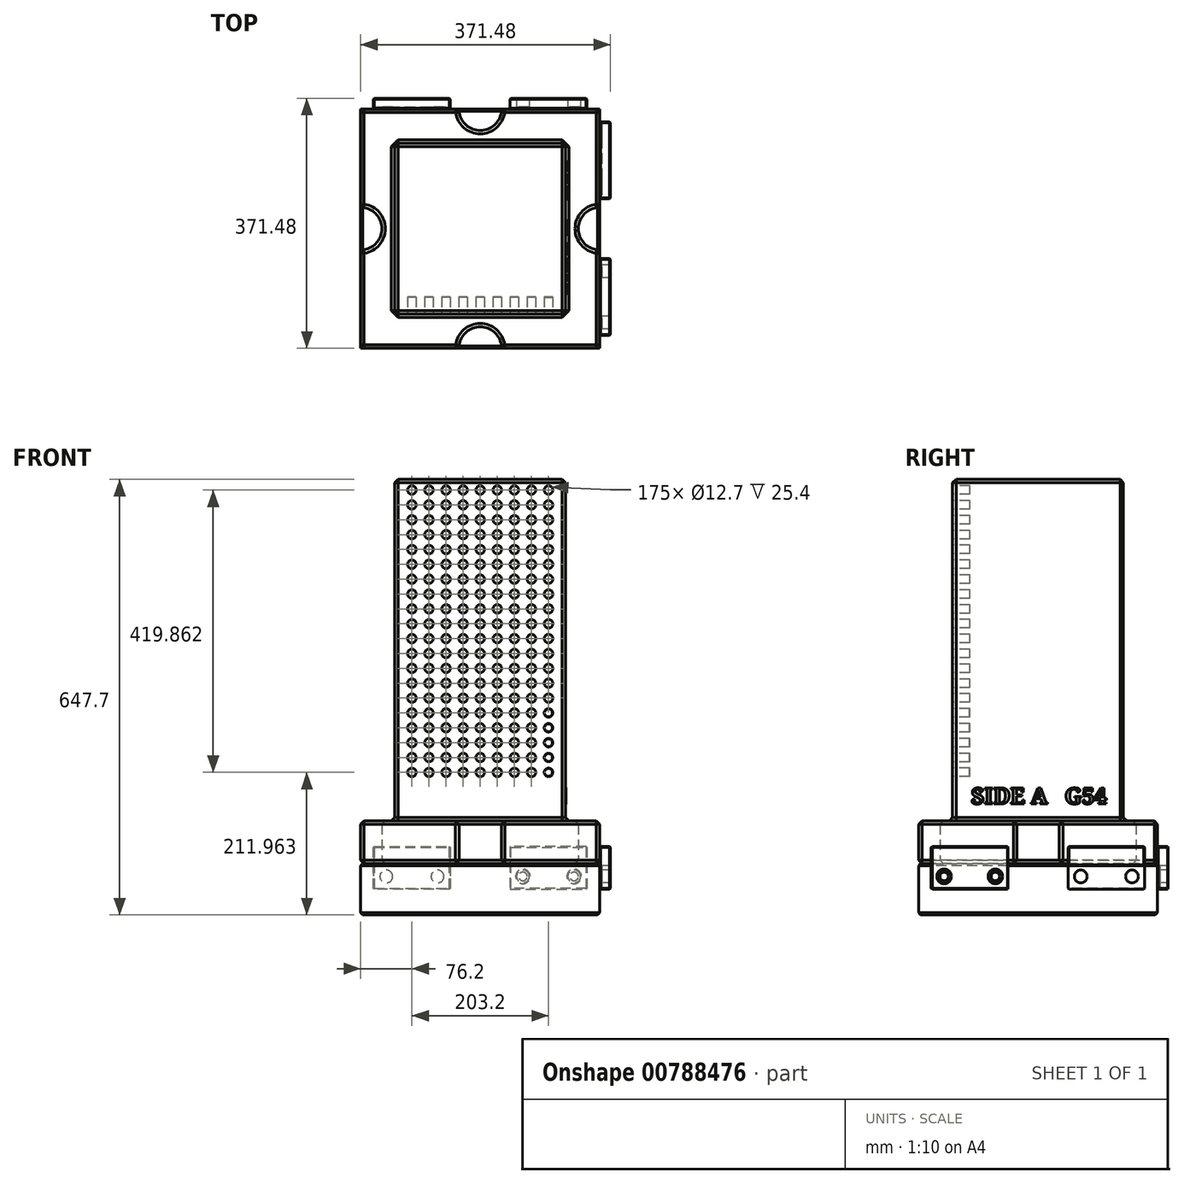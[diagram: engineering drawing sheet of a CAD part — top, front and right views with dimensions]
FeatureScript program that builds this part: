
annotation { "Feature Type Name" : "Feature", "Feature Type Description" : "" }
export const myFeature = defineFeature(function(context is Context, id is Id, definition is map)
    precondition{}
    {
        {
            var Q0;
            Q0=qCreatedBy(makeId("Top.planeOp"),FACE);
            var sketch = newSketch(context, id + "F0", { "sketchPlane" : qUnion([Q0])});
            skLineSegment(sketch, "E0.bottom", {"start": v(-127, -127) * mm, "end": v(127, -127) * mm});
            skLineSegment(sketch, "E0.top", {"start": v(-127, 127) * mm, "end": v(127, 127) * mm});
            skLineSegment(sketch, "E0.left", {"start": v(-127, -127) * mm, "end": v(-127, 127) * mm});
            skLineSegment(sketch, "E0.right", {"start": v(127, -127) * mm, "end": v(127, 127) * mm});
            skPoint(sketch, "E0.middle", {"position": v(0, 0) * mm});
            skLineSegment(sketch, "E1.bottom", {"start": v(-177.8, -177.8) * mm, "end": v(177.8, -177.8) * mm});
            skLineSegment(sketch, "E1.top", {"start": v(-177.8, 177.8) * mm, "end": v(177.8, 177.8) * mm});
            skLineSegment(sketch, "E1.left", {"start": v(-177.8, -177.8) * mm, "end": v(-177.8, 177.8) * mm});
            skLineSegment(sketch, "E1.right", {"start": v(177.8, -177.8) * mm, "end": v(177.8, 177.8) * mm});
            skSolve(sketch);
        }
        {
            var Q0;
            Q0=makeQuery(id+"F0.imprint","IMPRINT",FACE,{"disambiguationData":[TD([[makeQuery(id+"F0.imprint","IMPRINT",EDGE,{"derivedFrom":sQuery(id+"F0.wireOp",EDGE,"E0.bottom")}),1.0]])]});
            extrude(context, id + "F1", {"entities" : qUnion([Q0]), "depth" : 508 * mm});
        }
        {
            var Q0;
            Q0=makeQuery(id+"F0.imprint","IMPRINT",FACE,{"disambiguationData":[TD([[makeQuery(id+"F0.imprint","IMPRINT",EDGE,{"derivedFrom":sQuery(id+"F0.wireOp",EDGE,"E0.bottom")}),-1.0]])]});
            var Q1;
            Q1=makeQuery(id+"F0.imprint","IMPRINT",FACE,{"disambiguationData":[TD([[makeQuery(id+"F0.imprint","IMPRINT",EDGE,{"derivedFrom":sQuery(id+"F0.wireOp",EDGE,"E0.bottom")}),1.0]])]});
            extrude(context, id + "F2", {"entities" : qUnion([Q0, Q1]), "operationType" : NewBodyOperationType.ADD, "oppositeDirection" : true, "depth" : 63.5 * mm});
        }
        {
            var Q0;
            Q0=makeQuery(id+"F2.opExtrude","CAP_FACE",FACE,{"disambiguationData":[OSD([sQuery(id+"F0.wireOp",EDGE,"E1.bottom"),sQuery(id+"F0.wireOp",EDGE,"E1.top"),sQuery(id+"F0.wireOp",EDGE,"E1.left"),sQuery(id+"F0.wireOp",EDGE,"E1.right")])],"isStart":false});
            var sketch = newSketch(context, id + "F3", { "sketchPlane" : qUnion([Q0])});
            skCircle(sketch, "E2", {"center": v(-177.8, 0) * mm, "radius": 31.75 * mm});
            skCircle(sketch, "E3", {"center": v(177.8, 0) * mm, "radius": 31.75 * mm});
            skCircle(sketch, "E4", {"center": v(0, -177.8) * mm, "radius": 31.75 * mm});
            skCircle(sketch, "E5", {"center": v(0, 177.8) * mm, "radius": 31.75 * mm});
            skSolve(sketch);
        }
        {
            var Q0;
            {var subQ0=sQuery(id+"F3.wireOp",EDGE,"E5");var subQ1=makeQuery(id+"F2.opExtrude","CAP_EDGE",EDGE,{"disambiguationData":[OSD([sQuery(id+"F0.wireOp",EDGE,"E1.bottom")])],"isStart":false});var subQ2=makeQuery(id+"F3.imprint","INTERSECT",VERTEX,{"disambiguationData":[OD(0.0)],"derivedFrom":[subQ1,subQ0]});Q0=makeQuery(id+"F3.imprint","IMPRINT",FACE,{"disambiguationData":[TD([[makeQuery(id+"F3.imprint","IMPRINT",EDGE,{"disambiguationData":[TD([[subQ2,-1.0]])],"derivedFrom":subQ0}),1.0]])]});}
            var Q1;
            {var subQ0=sQuery(id+"F3.wireOp",EDGE,"E3");var subQ1=makeQuery(id+"F2.opExtrude","CAP_EDGE",EDGE,{"disambiguationData":[OSD([sQuery(id+"F0.wireOp",EDGE,"E1.right")])],"isStart":false});var subQ2=makeQuery(id+"F3.imprint","INTERSECT",VERTEX,{"disambiguationData":[OD(0.0)],"derivedFrom":[subQ1,subQ0]});Q1=makeQuery(id+"F3.imprint","IMPRINT",FACE,{"disambiguationData":[TD([[makeQuery(id+"F3.imprint","IMPRINT",EDGE,{"disambiguationData":[TD([[subQ2,-1.0]])],"derivedFrom":subQ0}),1.0]])]});}
            var Q2;
            {var subQ0=sQuery(id+"F3.wireOp",EDGE,"E2");var subQ1=makeQuery(id+"F2.opExtrude","CAP_EDGE",EDGE,{"disambiguationData":[OSD([sQuery(id+"F0.wireOp",EDGE,"E1.left")])],"isStart":false});var subQ2=makeQuery(id+"F3.imprint","INTERSECT",VERTEX,{"disambiguationData":[OD(0.0)],"derivedFrom":[subQ1,subQ0]});Q2=makeQuery(id+"F3.imprint","IMPRINT",FACE,{"disambiguationData":[TD([[makeQuery(id+"F3.imprint","IMPRINT",EDGE,{"disambiguationData":[TD([[subQ2,1.0]])],"derivedFrom":subQ0}),1.0]])]});}
            var Q3;
            {var subQ0=sQuery(id+"F3.wireOp",EDGE,"E4");var subQ1=makeQuery(id+"F2.opExtrude","CAP_EDGE",EDGE,{"disambiguationData":[OSD([sQuery(id+"F0.wireOp",EDGE,"E1.top")])],"isStart":false});var subQ2=makeQuery(id+"F3.imprint","INTERSECT",VERTEX,{"disambiguationData":[OD(0.0)],"derivedFrom":[subQ1,subQ0]});Q3=makeQuery(id+"F3.imprint","IMPRINT",FACE,{"disambiguationData":[TD([[makeQuery(id+"F3.imprint","IMPRINT",EDGE,{"disambiguationData":[TD([[subQ2,1.0]])],"derivedFrom":subQ0}),1.0]])]});}
            var Q4;
            Q4=makeQuery(id+"F2.opExtrude","CAP_FACE",FACE,{"disambiguationData":[OSD([sQuery(id+"F0.wireOp",EDGE,"E1.bottom"),sQuery(id+"F0.wireOp",EDGE,"E1.top"),sQuery(id+"F0.wireOp",EDGE,"E1.left"),sQuery(id+"F0.wireOp",EDGE,"E1.right")])],"isStart":true});
            extrude(context, id + "F4", {"entities" : qUnion([Q0, Q1, Q2, Q3]), "operationType" : NewBodyOperationType.REMOVE, "endBound" : BoundingType.UP_TO_SURFACE, "oppositeDirection" : true, "endBoundEntityFace" : qUnion([Q4]), "depth" : 25.4 * mm});
        }
        {
            var Q0;
            Q0=makeQuery(id+"F1.opExtrude","CAP_FACE",FACE,{"disambiguationData":[OSD([sQuery(id+"F0.wireOp",EDGE,"E0.bottom"),sQuery(id+"F0.wireOp",EDGE,"E0.top"),sQuery(id+"F0.wireOp",EDGE,"E0.left"),sQuery(id+"F0.wireOp",EDGE,"E0.right")])],"isStart":false});
            var Q1;
            Q1=makeQuery(id+"F1.opExtrude","SWEPT_FACE",FACE,{"disambiguationData":[OSD([sQuery(id+"F0.wireOp",EDGE,"E0.right")])]});
            var Q2;
            Q2=makeQuery(id+"F1.opExtrude","SWEPT_FACE",FACE,{"disambiguationData":[OSD([sQuery(id+"F0.wireOp",EDGE,"E0.top")])]});
            var Q3;
            Q3=makeQuery(id+"F1.opExtrude","SWEPT_FACE",FACE,{"disambiguationData":[OSD([sQuery(id+"F0.wireOp",EDGE,"E0.left")])]});
            var Q4;
            Q4=makeQuery(id+"F1.opExtrude","SWEPT_FACE",FACE,{"disambiguationData":[OSD([sQuery(id+"F0.wireOp",EDGE,"E0.bottom")])]});
            var Q5;
            {var subQ1=sQuery(id+"F0.wireOp",EDGE,"E1.left");var subQ3=sQuery(id+"F0.wireOp",EDGE,"E1.bottom");Q5=makeQuery(id+"F4.boolean.opBoolean","SPLIT",FACE,{"disambiguationData":[TD([makeQuery(id+"F2.opExtrude","SWEPT_FACE",FACE,{"disambiguationData":[OSD([subQ1])]})])],"derivedFrom":makeQuery(id+"F2.opExtrude","SWEPT_FACE",FACE,{"disambiguationData":[OSD([subQ3])]})});}
            var Q6;
            {var subQ0=sQuery(id+"F0.wireOp",EDGE,"E1.right");var subQ3=sQuery(id+"F0.wireOp",EDGE,"E1.bottom");Q6=makeQuery(id+"F4.boolean.opBoolean","SPLIT",FACE,{"disambiguationData":[TD([makeQuery(id+"F2.opExtrude","SWEPT_FACE",FACE,{"disambiguationData":[OSD([subQ0])]})])],"derivedFrom":makeQuery(id+"F2.opExtrude","SWEPT_FACE",FACE,{"disambiguationData":[OSD([subQ3])]})});}
            var Q7;
            Q7=makeQuery(id+"F4.boolean.opBoolean","COPY",FACE,{"derivedFrom":makeQuery(id+"F4.opExtrude","SWEPT_FACE",FACE,{"disambiguationData":[OSD([sQuery(id+"F3.wireOp",EDGE,"E5")])]})});
            var Q8;
            Q8=makeQuery(id+"F4.boolean.opBoolean","COPY",FACE,{"derivedFrom":makeQuery(id+"F4.opExtrude","SWEPT_FACE",FACE,{"disambiguationData":[OSD([sQuery(id+"F3.wireOp",EDGE,"E3")])]})});
            var Q9;
            {var subQ0=sQuery(id+"F0.wireOp",EDGE,"E1.bottom");var subQ1=sQuery(id+"F0.wireOp",EDGE,"E1.right");Q9=makeQuery(id+"F4.boolean.opBoolean","SPLIT",FACE,{"disambiguationData":[TD([makeQuery(id+"F2.opExtrude","SWEPT_FACE",FACE,{"disambiguationData":[OSD([subQ0])]})])],"derivedFrom":makeQuery(id+"F2.opExtrude","SWEPT_FACE",FACE,{"disambiguationData":[OSD([subQ1])]})});}
            var Q10;
            {var subQ0=sQuery(id+"F0.wireOp",EDGE,"E1.right");var subQ2=sQuery(id+"F0.wireOp",EDGE,"E1.top");Q10=makeQuery(id+"F4.boolean.opBoolean","SPLIT",FACE,{"disambiguationData":[TD([makeQuery(id+"F2.opExtrude","SWEPT_FACE",FACE,{"disambiguationData":[OSD([subQ2])]})])],"derivedFrom":makeQuery(id+"F2.opExtrude","SWEPT_FACE",FACE,{"disambiguationData":[OSD([subQ0])]})});}
            var Q11;
            {var subQ0=sQuery(id+"F0.wireOp",EDGE,"E1.right");var subQ2=sQuery(id+"F0.wireOp",EDGE,"E1.top");Q11=makeQuery(id+"F4.boolean.opBoolean","SPLIT",FACE,{"disambiguationData":[TD([makeQuery(id+"F2.opExtrude","SWEPT_FACE",FACE,{"disambiguationData":[OSD([subQ0])]})])],"derivedFrom":makeQuery(id+"F2.opExtrude","SWEPT_FACE",FACE,{"disambiguationData":[OSD([subQ2])]})});}
            var Q12;
            Q12=makeQuery(id+"F4.boolean.opBoolean","COPY",FACE,{"derivedFrom":makeQuery(id+"F4.opExtrude","SWEPT_FACE",FACE,{"disambiguationData":[OSD([sQuery(id+"F3.wireOp",EDGE,"E4")])]})});
            var Q13;
            {var subQ1=sQuery(id+"F0.wireOp",EDGE,"E1.left");var subQ2=sQuery(id+"F0.wireOp",EDGE,"E1.top");Q13=makeQuery(id+"F4.boolean.opBoolean","SPLIT",FACE,{"disambiguationData":[TD([makeQuery(id+"F2.opExtrude","SWEPT_FACE",FACE,{"disambiguationData":[OSD([subQ1])]})])],"derivedFrom":makeQuery(id+"F2.opExtrude","SWEPT_FACE",FACE,{"disambiguationData":[OSD([subQ2])]})});}
            var Q14;
            {var subQ1=sQuery(id+"F0.wireOp",EDGE,"E1.left");var subQ2=sQuery(id+"F0.wireOp",EDGE,"E1.top");Q14=makeQuery(id+"F4.boolean.opBoolean","SPLIT",FACE,{"disambiguationData":[TD([makeQuery(id+"F2.opExtrude","SWEPT_FACE",FACE,{"disambiguationData":[OSD([subQ2])]})])],"derivedFrom":makeQuery(id+"F2.opExtrude","SWEPT_FACE",FACE,{"disambiguationData":[OSD([subQ1])]})});}
            var Q15;
            Q15=makeQuery(id+"F4.boolean.opBoolean","COPY",FACE,{"derivedFrom":makeQuery(id+"F4.opExtrude","SWEPT_FACE",FACE,{"disambiguationData":[OSD([sQuery(id+"F3.wireOp",EDGE,"E2")])]})});
            var Q16;
            {var subQ0=sQuery(id+"F0.wireOp",EDGE,"E1.bottom");var subQ2=sQuery(id+"F0.wireOp",EDGE,"E1.left");Q16=makeQuery(id+"F4.boolean.opBoolean","SPLIT",FACE,{"disambiguationData":[TD([makeQuery(id+"F2.opExtrude","SWEPT_FACE",FACE,{"disambiguationData":[OSD([subQ0])]})])],"derivedFrom":makeQuery(id+"F2.opExtrude","SWEPT_FACE",FACE,{"disambiguationData":[OSD([subQ2])]})});}
            chamfer(context, id + "F5", {"entities" : qUnion([Q0, Q1, Q2, Q3, Q4, Q5, Q6, Q7, Q8, Q9, Q10, Q11, Q12, Q13, Q14, Q15, Q16]), "width" : 5.08 * mm, "tangentPropagation" : true});
        }
        {
            var Q0;
            Q0=makeQuery(id+"F1.opExtrude","SWEPT_FACE",FACE,{"disambiguationData":[OSD([sQuery(id+"F0.wireOp",EDGE,"E0.bottom")])]});
            var sketch = newSketch(context, id + "F6", { "sketchPlane" : qUnion([Q0])});
            skCircle(sketch, "E6", {"center": v(-101.6, 492.13) * mm, "radius": 6.35 * mm});
            skLineSegment(sketch, "E7", {"start": v(0, 0) * mm, "end": v(0, 678.57) * mm, "construction": true});
            skCircle(sketch, "E8.0.1.0", {"center": v(-101.6, 470.03) * mm, "radius": 6.35 * mm});
            skCircle(sketch, "E8.0.2.0", {"center": v(-101.6, 447.93) * mm, "radius": 6.35 * mm});
            skCircle(sketch, "E8.0.3.0", {"center": v(-101.6, 425.83) * mm, "radius": 6.35 * mm});
            skCircle(sketch, "E8.0.4.0", {"center": v(-101.6, 403.73) * mm, "radius": 6.35 * mm});
            skCircle(sketch, "E8.0.5.0", {"center": v(-101.6, 381.63) * mm, "radius": 6.35 * mm});
            skCircle(sketch, "E8.0.6.0", {"center": v(-101.6, 359.54) * mm, "radius": 6.35 * mm});
            skCircle(sketch, "E8.0.7.0", {"center": v(-101.6, 337.44) * mm, "radius": 6.35 * mm});
            skCircle(sketch, "E8.0.8.0", {"center": v(-101.6, 315.34) * mm, "radius": 6.35 * mm});
            skCircle(sketch, "E8.0.9.0", {"center": v(-101.6, 293.24) * mm, "radius": 6.35 * mm});
            skCircle(sketch, "E8.0.10.0", {"center": v(-101.6, 271.14) * mm, "radius": 6.35 * mm});
            skCircle(sketch, "E8.0.11.0", {"center": v(-101.6, 249.05) * mm, "radius": 6.35 * mm});
            skCircle(sketch, "E8.0.12.0", {"center": v(-101.6, 226.95) * mm, "radius": 6.35 * mm});
            skCircle(sketch, "E8.0.13.0", {"center": v(-101.6, 204.85) * mm, "radius": 6.35 * mm});
            skCircle(sketch, "E8.0.14.0", {"center": v(-101.6, 182.75) * mm, "radius": 6.35 * mm});
            skCircle(sketch, "E8.1.0.0", {"center": v(-76.2, 492.13) * mm, "radius": 6.35 * mm});
            skCircle(sketch, "E8.1.1.0", {"center": v(-76.2, 470.03) * mm, "radius": 6.35 * mm});
            skCircle(sketch, "E8.1.2.0", {"center": v(-76.2, 447.93) * mm, "radius": 6.35 * mm});
            skCircle(sketch, "E8.1.3.0", {"center": v(-76.2, 425.83) * mm, "radius": 6.35 * mm});
            skCircle(sketch, "E8.1.4.0", {"center": v(-76.2, 403.73) * mm, "radius": 6.35 * mm});
            skCircle(sketch, "E8.1.5.0", {"center": v(-76.2, 381.63) * mm, "radius": 6.35 * mm});
            skCircle(sketch, "E8.1.6.0", {"center": v(-76.2, 359.54) * mm, "radius": 6.35 * mm});
            skCircle(sketch, "E8.1.7.0", {"center": v(-76.2, 337.44) * mm, "radius": 6.35 * mm});
            skCircle(sketch, "E8.1.8.0", {"center": v(-76.2, 315.34) * mm, "radius": 6.35 * mm});
            skCircle(sketch, "E8.1.9.0", {"center": v(-76.2, 293.24) * mm, "radius": 6.35 * mm});
            skCircle(sketch, "E8.1.10.0", {"center": v(-76.2, 271.14) * mm, "radius": 6.35 * mm});
            skCircle(sketch, "E8.1.11.0", {"center": v(-76.2, 249.05) * mm, "radius": 6.35 * mm});
            skCircle(sketch, "E8.1.12.0", {"center": v(-76.2, 226.95) * mm, "radius": 6.35 * mm});
            skCircle(sketch, "E8.1.13.0", {"center": v(-76.2, 204.85) * mm, "radius": 6.35 * mm});
            skCircle(sketch, "E8.1.14.0", {"center": v(-76.2, 182.75) * mm, "radius": 6.35 * mm});
            skCircle(sketch, "E8.2.0.0", {"center": v(-50.8, 492.13) * mm, "radius": 6.35 * mm});
            skCircle(sketch, "E8.2.1.0", {"center": v(-50.8, 470.03) * mm, "radius": 6.35 * mm});
            skCircle(sketch, "E8.2.2.0", {"center": v(-50.8, 447.93) * mm, "radius": 6.35 * mm});
            skCircle(sketch, "E8.2.3.0", {"center": v(-50.8, 425.83) * mm, "radius": 6.35 * mm});
            skCircle(sketch, "E8.2.4.0", {"center": v(-50.8, 403.73) * mm, "radius": 6.35 * mm});
            skCircle(sketch, "E8.2.5.0", {"center": v(-50.8, 381.63) * mm, "radius": 6.35 * mm});
            skCircle(sketch, "E8.2.6.0", {"center": v(-50.8, 359.54) * mm, "radius": 6.35 * mm});
            skCircle(sketch, "E8.2.7.0", {"center": v(-50.8, 337.44) * mm, "radius": 6.35 * mm});
            skCircle(sketch, "E8.2.8.0", {"center": v(-50.8, 315.34) * mm, "radius": 6.35 * mm});
            skCircle(sketch, "E8.2.9.0", {"center": v(-50.8, 293.24) * mm, "radius": 6.35 * mm});
            skCircle(sketch, "E8.2.10.0", {"center": v(-50.8, 271.14) * mm, "radius": 6.35 * mm});
            skCircle(sketch, "E8.2.11.0", {"center": v(-50.8, 249.05) * mm, "radius": 6.35 * mm});
            skCircle(sketch, "E8.2.12.0", {"center": v(-50.8, 226.95) * mm, "radius": 6.35 * mm});
            skCircle(sketch, "E8.2.13.0", {"center": v(-50.8, 204.85) * mm, "radius": 6.35 * mm});
            skCircle(sketch, "E8.2.14.0", {"center": v(-50.8, 182.75) * mm, "radius": 6.35 * mm});
            skCircle(sketch, "E8.3.0.0", {"center": v(-25.4, 492.13) * mm, "radius": 6.35 * mm});
            skCircle(sketch, "E8.3.1.0", {"center": v(-25.4, 470.03) * mm, "radius": 6.35 * mm});
            skCircle(sketch, "E8.3.2.0", {"center": v(-25.4, 447.93) * mm, "radius": 6.35 * mm});
            skCircle(sketch, "E8.3.3.0", {"center": v(-25.4, 425.83) * mm, "radius": 6.35 * mm});
            skCircle(sketch, "E8.3.4.0", {"center": v(-25.4, 403.73) * mm, "radius": 6.35 * mm});
            skCircle(sketch, "E8.3.5.0", {"center": v(-25.4, 381.63) * mm, "radius": 6.35 * mm});
            skCircle(sketch, "E8.3.6.0", {"center": v(-25.4, 359.54) * mm, "radius": 6.35 * mm});
            skCircle(sketch, "E8.3.7.0", {"center": v(-25.4, 337.44) * mm, "radius": 6.35 * mm});
            skCircle(sketch, "E8.3.8.0", {"center": v(-25.4, 315.34) * mm, "radius": 6.35 * mm});
            skCircle(sketch, "E8.3.9.0", {"center": v(-25.4, 293.24) * mm, "radius": 6.35 * mm});
            skCircle(sketch, "E8.3.10.0", {"center": v(-25.4, 271.14) * mm, "radius": 6.35 * mm});
            skCircle(sketch, "E8.3.11.0", {"center": v(-25.4, 249.05) * mm, "radius": 6.35 * mm});
            skCircle(sketch, "E8.3.12.0", {"center": v(-25.4, 226.95) * mm, "radius": 6.35 * mm});
            skCircle(sketch, "E8.3.13.0", {"center": v(-25.4, 204.85) * mm, "radius": 6.35 * mm});
            skCircle(sketch, "E8.3.14.0", {"center": v(-25.4, 182.75) * mm, "radius": 6.35 * mm});
            skCircle(sketch, "E8.4.0.0", {"center": v(0, 492.13) * mm, "radius": 6.35 * mm});
            skCircle(sketch, "E8.4.1.0", {"center": v(0, 470.03) * mm, "radius": 6.35 * mm});
            skCircle(sketch, "E8.4.2.0", {"center": v(0, 447.93) * mm, "radius": 6.35 * mm});
            skCircle(sketch, "E8.4.3.0", {"center": v(0, 425.83) * mm, "radius": 6.35 * mm});
            skCircle(sketch, "E8.4.4.0", {"center": v(0, 403.73) * mm, "radius": 6.35 * mm});
            skCircle(sketch, "E8.4.5.0", {"center": v(0, 381.63) * mm, "radius": 6.35 * mm});
            skCircle(sketch, "E8.4.6.0", {"center": v(0, 359.54) * mm, "radius": 6.35 * mm});
            skCircle(sketch, "E8.4.7.0", {"center": v(0, 337.44) * mm, "radius": 6.35 * mm});
            skCircle(sketch, "E8.4.8.0", {"center": v(0, 315.34) * mm, "radius": 6.35 * mm});
            skCircle(sketch, "E8.4.9.0", {"center": v(0, 293.24) * mm, "radius": 6.35 * mm});
            skCircle(sketch, "E8.4.10.0", {"center": v(0, 271.14) * mm, "radius": 6.35 * mm});
            skCircle(sketch, "E8.4.11.0", {"center": v(0, 249.05) * mm, "radius": 6.35 * mm});
            skCircle(sketch, "E8.4.12.0", {"center": v(0, 226.95) * mm, "radius": 6.35 * mm});
            skCircle(sketch, "E8.4.13.0", {"center": v(0, 204.85) * mm, "radius": 6.35 * mm});
            skCircle(sketch, "E8.4.14.0", {"center": v(0, 182.75) * mm, "radius": 6.35 * mm});
            skCircle(sketch, "E8.5.0.0", {"center": v(25.4, 492.13) * mm, "radius": 6.35 * mm});
            skCircle(sketch, "E8.5.1.0", {"center": v(25.4, 470.03) * mm, "radius": 6.35 * mm});
            skCircle(sketch, "E8.5.2.0", {"center": v(25.4, 447.93) * mm, "radius": 6.35 * mm});
            skCircle(sketch, "E8.5.3.0", {"center": v(25.4, 425.83) * mm, "radius": 6.35 * mm});
            skCircle(sketch, "E8.5.4.0", {"center": v(25.4, 403.73) * mm, "radius": 6.35 * mm});
            skCircle(sketch, "E8.5.5.0", {"center": v(25.4, 381.63) * mm, "radius": 6.35 * mm});
            skCircle(sketch, "E8.5.6.0", {"center": v(25.4, 359.54) * mm, "radius": 6.35 * mm});
            skCircle(sketch, "E8.5.7.0", {"center": v(25.4, 337.44) * mm, "radius": 6.35 * mm});
            skCircle(sketch, "E8.5.8.0", {"center": v(25.4, 315.34) * mm, "radius": 6.35 * mm});
            skCircle(sketch, "E8.5.9.0", {"center": v(25.4, 293.24) * mm, "radius": 6.35 * mm});
            skCircle(sketch, "E8.5.10.0", {"center": v(25.4, 271.14) * mm, "radius": 6.35 * mm});
            skCircle(sketch, "E8.5.11.0", {"center": v(25.4, 249.05) * mm, "radius": 6.35 * mm});
            skCircle(sketch, "E8.5.12.0", {"center": v(25.4, 226.95) * mm, "radius": 6.35 * mm});
            skCircle(sketch, "E8.5.13.0", {"center": v(25.4, 204.85) * mm, "radius": 6.35 * mm});
            skCircle(sketch, "E8.5.14.0", {"center": v(25.4, 182.75) * mm, "radius": 6.35 * mm});
            skCircle(sketch, "E8.6.0.0", {"center": v(50.8, 492.13) * mm, "radius": 6.35 * mm});
            skCircle(sketch, "E8.6.1.0", {"center": v(50.8, 470.03) * mm, "radius": 6.35 * mm});
            skCircle(sketch, "E8.6.2.0", {"center": v(50.8, 447.93) * mm, "radius": 6.35 * mm});
            skCircle(sketch, "E8.6.3.0", {"center": v(50.8, 425.83) * mm, "radius": 6.35 * mm});
            skCircle(sketch, "E8.6.4.0", {"center": v(50.8, 403.73) * mm, "radius": 6.35 * mm});
            skCircle(sketch, "E8.6.5.0", {"center": v(50.8, 381.63) * mm, "radius": 6.35 * mm});
            skCircle(sketch, "E8.6.6.0", {"center": v(50.8, 359.54) * mm, "radius": 6.35 * mm});
            skCircle(sketch, "E8.6.7.0", {"center": v(50.8, 337.44) * mm, "radius": 6.35 * mm});
            skCircle(sketch, "E8.6.8.0", {"center": v(50.8, 315.34) * mm, "radius": 6.35 * mm});
            skCircle(sketch, "E8.6.9.0", {"center": v(50.8, 293.24) * mm, "radius": 6.35 * mm});
            skCircle(sketch, "E8.6.10.0", {"center": v(50.8, 271.14) * mm, "radius": 6.35 * mm});
            skCircle(sketch, "E8.6.11.0", {"center": v(50.8, 249.05) * mm, "radius": 6.35 * mm});
            skCircle(sketch, "E8.6.12.0", {"center": v(50.8, 226.95) * mm, "radius": 6.35 * mm});
            skCircle(sketch, "E8.6.13.0", {"center": v(50.8, 204.85) * mm, "radius": 6.35 * mm});
            skCircle(sketch, "E8.6.14.0", {"center": v(50.8, 182.75) * mm, "radius": 6.35 * mm});
            skCircle(sketch, "E8.7.0.0", {"center": v(76.2, 492.13) * mm, "radius": 6.35 * mm});
            skCircle(sketch, "E8.7.1.0", {"center": v(76.2, 470.03) * mm, "radius": 6.35 * mm});
            skCircle(sketch, "E8.7.2.0", {"center": v(76.2, 447.93) * mm, "radius": 6.35 * mm});
            skCircle(sketch, "E8.7.3.0", {"center": v(76.2, 425.83) * mm, "radius": 6.35 * mm});
            skCircle(sketch, "E8.7.4.0", {"center": v(76.2, 403.73) * mm, "radius": 6.35 * mm});
            skCircle(sketch, "E8.7.5.0", {"center": v(76.2, 381.63) * mm, "radius": 6.35 * mm});
            skCircle(sketch, "E8.7.6.0", {"center": v(76.2, 359.54) * mm, "radius": 6.35 * mm});
            skCircle(sketch, "E8.7.7.0", {"center": v(76.2, 337.44) * mm, "radius": 6.35 * mm});
            skCircle(sketch, "E8.7.8.0", {"center": v(76.2, 315.34) * mm, "radius": 6.35 * mm});
            skCircle(sketch, "E8.7.9.0", {"center": v(76.2, 293.24) * mm, "radius": 6.35 * mm});
            skCircle(sketch, "E8.7.10.0", {"center": v(76.2, 271.14) * mm, "radius": 6.35 * mm});
            skCircle(sketch, "E8.7.11.0", {"center": v(76.2, 249.05) * mm, "radius": 6.35 * mm});
            skCircle(sketch, "E8.7.12.0", {"center": v(76.2, 226.95) * mm, "radius": 6.35 * mm});
            skCircle(sketch, "E8.7.13.0", {"center": v(76.2, 204.85) * mm, "radius": 6.35 * mm});
            skCircle(sketch, "E8.7.14.0", {"center": v(76.2, 182.75) * mm, "radius": 6.35 * mm});
            skCircle(sketch, "E8.8.0.0", {"center": v(101.6, 492.13) * mm, "radius": 6.35 * mm});
            skCircle(sketch, "E8.8.1.0", {"center": v(101.6, 470.03) * mm, "radius": 6.35 * mm});
            skCircle(sketch, "E8.8.2.0", {"center": v(101.6, 447.93) * mm, "radius": 6.35 * mm});
            skCircle(sketch, "E8.8.3.0", {"center": v(101.6, 425.83) * mm, "radius": 6.35 * mm});
            skCircle(sketch, "E8.8.4.0", {"center": v(101.6, 403.73) * mm, "radius": 6.35 * mm});
            skCircle(sketch, "E8.8.5.0", {"center": v(101.6, 381.63) * mm, "radius": 6.35 * mm});
            skCircle(sketch, "E8.8.6.0", {"center": v(101.6, 359.54) * mm, "radius": 6.35 * mm});
            skCircle(sketch, "E8.8.7.0", {"center": v(101.6, 337.44) * mm, "radius": 6.35 * mm});
            skCircle(sketch, "E8.8.8.0", {"center": v(101.6, 315.34) * mm, "radius": 6.35 * mm});
            skCircle(sketch, "E8.8.9.0", {"center": v(101.6, 293.24) * mm, "radius": 6.35 * mm});
            skCircle(sketch, "E8.8.10.0", {"center": v(101.6, 271.14) * mm, "radius": 6.35 * mm});
            skCircle(sketch, "E8.8.11.0", {"center": v(101.6, 249.05) * mm, "radius": 6.35 * mm});
            skCircle(sketch, "E8.8.12.0", {"center": v(101.6, 226.95) * mm, "radius": 6.35 * mm});
            skCircle(sketch, "E8.8.13.0", {"center": v(101.6, 204.85) * mm, "radius": 6.35 * mm});
            skCircle(sketch, "E8.8.14.0", {"center": v(101.6, 182.75) * mm, "radius": 6.35 * mm});
            skLineSegment(sketch, "E8.direction1", {"start": v(-101.6, 492.13) * mm, "end": v(-76.2, 492.13) * mm, "construction": true});
            skLineSegment(sketch, "E8.direction2", {"start": v(-101.6, 492.13) * mm, "end": v(-101.6, 470.03) * mm, "construction": true});
            skCircle(sketch, "E9.0.0.15", {"center": v(-101.6, 160.65) * mm, "radius": 6.35 * mm});
            skCircle(sketch, "E9.0.0.16", {"center": v(-101.6, 138.56) * mm, "radius": 6.35 * mm});
            skCircle(sketch, "E9.0.0.17", {"center": v(-101.6, 116.46) * mm, "radius": 6.35 * mm});
            skCircle(sketch, "E9.0.0.18", {"center": v(-101.6, 94.36) * mm, "radius": 6.35 * mm});
            skCircle(sketch, "E9.0.0.19", {"center": v(-101.6, 72.26) * mm, "radius": 6.35 * mm});
            skCircle(sketch, "E9.0.1.15", {"center": v(-76.2, 160.65) * mm, "radius": 6.35 * mm});
            skCircle(sketch, "E9.0.1.16", {"center": v(-76.2, 138.56) * mm, "radius": 6.35 * mm});
            skCircle(sketch, "E9.0.1.17", {"center": v(-76.2, 116.46) * mm, "radius": 6.35 * mm});
            skCircle(sketch, "E9.0.1.18", {"center": v(-76.2, 94.36) * mm, "radius": 6.35 * mm});
            skCircle(sketch, "E9.0.1.19", {"center": v(-76.2, 72.26) * mm, "radius": 6.35 * mm});
            skCircle(sketch, "E9.0.2.15", {"center": v(-50.8, 160.65) * mm, "radius": 6.35 * mm});
            skCircle(sketch, "E9.0.2.16", {"center": v(-50.8, 138.56) * mm, "radius": 6.35 * mm});
            skCircle(sketch, "E9.0.2.17", {"center": v(-50.8, 116.46) * mm, "radius": 6.35 * mm});
            skCircle(sketch, "E9.0.2.18", {"center": v(-50.8, 94.36) * mm, "radius": 6.35 * mm});
            skCircle(sketch, "E9.0.2.19", {"center": v(-50.8, 72.26) * mm, "radius": 6.35 * mm});
            skCircle(sketch, "E9.0.3.15", {"center": v(-25.4, 160.65) * mm, "radius": 6.35 * mm});
            skCircle(sketch, "E9.0.3.16", {"center": v(-25.4, 138.56) * mm, "radius": 6.35 * mm});
            skCircle(sketch, "E9.0.3.17", {"center": v(-25.4, 116.46) * mm, "radius": 6.35 * mm});
            skCircle(sketch, "E9.0.3.18", {"center": v(-25.4, 94.36) * mm, "radius": 6.35 * mm});
            skCircle(sketch, "E9.0.3.19", {"center": v(-25.4, 72.26) * mm, "radius": 6.35 * mm});
            skCircle(sketch, "E9.0.4.15", {"center": v(0, 160.65) * mm, "radius": 6.35 * mm});
            skCircle(sketch, "E9.0.4.16", {"center": v(0, 138.56) * mm, "radius": 6.35 * mm});
            skCircle(sketch, "E9.0.4.17", {"center": v(0, 116.46) * mm, "radius": 6.35 * mm});
            skCircle(sketch, "E9.0.4.18", {"center": v(0, 94.36) * mm, "radius": 6.35 * mm});
            skCircle(sketch, "E9.0.4.19", {"center": v(0, 72.26) * mm, "radius": 6.35 * mm});
            skCircle(sketch, "E9.0.5.15", {"center": v(25.4, 160.65) * mm, "radius": 6.35 * mm});
            skCircle(sketch, "E9.0.5.16", {"center": v(25.4, 138.56) * mm, "radius": 6.35 * mm});
            skCircle(sketch, "E9.0.5.17", {"center": v(25.4, 116.46) * mm, "radius": 6.35 * mm});
            skCircle(sketch, "E9.0.5.18", {"center": v(25.4, 94.36) * mm, "radius": 6.35 * mm});
            skCircle(sketch, "E9.0.5.19", {"center": v(25.4, 72.26) * mm, "radius": 6.35 * mm});
            skCircle(sketch, "E9.0.6.15", {"center": v(50.8, 160.65) * mm, "radius": 6.35 * mm});
            skCircle(sketch, "E9.0.6.16", {"center": v(50.8, 138.56) * mm, "radius": 6.35 * mm});
            skCircle(sketch, "E9.0.6.17", {"center": v(50.8, 116.46) * mm, "radius": 6.35 * mm});
            skCircle(sketch, "E9.0.6.18", {"center": v(50.8, 94.36) * mm, "radius": 6.35 * mm});
            skCircle(sketch, "E9.0.6.19", {"center": v(50.8, 72.26) * mm, "radius": 6.35 * mm});
            skCircle(sketch, "E9.0.7.15", {"center": v(76.2, 160.65) * mm, "radius": 6.35 * mm});
            skCircle(sketch, "E9.0.7.16", {"center": v(76.2, 138.56) * mm, "radius": 6.35 * mm});
            skCircle(sketch, "E9.0.7.17", {"center": v(76.2, 116.46) * mm, "radius": 6.35 * mm});
            skCircle(sketch, "E9.0.7.18", {"center": v(76.2, 94.36) * mm, "radius": 6.35 * mm});
            skCircle(sketch, "E9.0.7.19", {"center": v(76.2, 72.26) * mm, "radius": 6.35 * mm});
            skCircle(sketch, "E9.0.8.15", {"center": v(101.6, 160.65) * mm, "radius": 6.35 * mm});
            skCircle(sketch, "E9.0.8.16", {"center": v(101.6, 138.56) * mm, "radius": 6.35 * mm});
            skCircle(sketch, "E9.0.8.17", {"center": v(101.6, 116.46) * mm, "radius": 6.35 * mm});
            skCircle(sketch, "E9.0.8.18", {"center": v(101.6, 94.36) * mm, "radius": 6.35 * mm});
            skCircle(sketch, "E9.0.8.19", {"center": v(101.6, 72.26) * mm, "radius": 6.35 * mm});
            skSolve(sketch);
        }
        {
            var Q0;
            Q0=qSketchRegion(id+"F6",true);
            extrude(context, id + "F7", {"entities" : qUnion([Q0]), "operationType" : NewBodyOperationType.REMOVE, "oppositeDirection" : true, "depth" : 25.4 * mm});
        }
        {
            var Q0;
            Q0=makeQuery(id+"F7.boolean.opBoolean","COPY",EDGE,{"derivedFrom":makeQuery(id+"F7.opExtrude","CAP_EDGE",EDGE,{"disambiguationData":[OSD([sQuery(id+"F6.wireOp",EDGE,"E6")])],"isStart":true})});
            var Q1;
            Q1=makeQuery(id+"F7.boolean.opBoolean","COPY",EDGE,{"derivedFrom":makeQuery(id+"F7.opExtrude","CAP_EDGE",EDGE,{"disambiguationData":[OSD([sQuery(id+"F6.wireOp",EDGE,"E8.0.1.0")])],"isStart":true})});
            var Q2;
            Q2=makeQuery(id+"F7.boolean.opBoolean","COPY",EDGE,{"derivedFrom":makeQuery(id+"F7.opExtrude","CAP_EDGE",EDGE,{"disambiguationData":[OSD([sQuery(id+"F6.wireOp",EDGE,"E8.0.2.0")])],"isStart":true})});
            var Q3;
            Q3=makeQuery(id+"F7.boolean.opBoolean","COPY",EDGE,{"derivedFrom":makeQuery(id+"F7.opExtrude","CAP_EDGE",EDGE,{"disambiguationData":[OSD([sQuery(id+"F6.wireOp",EDGE,"E8.0.3.0")])],"isStart":true})});
            var Q4;
            Q4=makeQuery(id+"F7.boolean.opBoolean","COPY",EDGE,{"derivedFrom":makeQuery(id+"F7.opExtrude","CAP_EDGE",EDGE,{"disambiguationData":[OSD([sQuery(id+"F6.wireOp",EDGE,"E8.0.4.0")])],"isStart":true})});
            var Q5;
            Q5=makeQuery(id+"F7.boolean.opBoolean","COPY",EDGE,{"derivedFrom":makeQuery(id+"F7.opExtrude","CAP_EDGE",EDGE,{"disambiguationData":[OSD([sQuery(id+"F6.wireOp",EDGE,"E8.0.6.0")])],"isStart":true})});
            var Q6;
            Q6=makeQuery(id+"F7.boolean.opBoolean","COPY",EDGE,{"derivedFrom":makeQuery(id+"F7.opExtrude","CAP_EDGE",EDGE,{"disambiguationData":[OSD([sQuery(id+"F6.wireOp",EDGE,"E8.0.5.0")])],"isStart":true})});
            var Q7;
            Q7=makeQuery(id+"F7.boolean.opBoolean","COPY",EDGE,{"derivedFrom":makeQuery(id+"F7.opExtrude","CAP_EDGE",EDGE,{"disambiguationData":[OSD([sQuery(id+"F6.wireOp",EDGE,"E8.0.7.0")])],"isStart":true})});
            var Q8;
            Q8=makeQuery(id+"F7.boolean.opBoolean","COPY",EDGE,{"derivedFrom":makeQuery(id+"F7.opExtrude","CAP_EDGE",EDGE,{"disambiguationData":[OSD([sQuery(id+"F6.wireOp",EDGE,"E8.0.8.0")])],"isStart":true})});
            var Q9;
            Q9=makeQuery(id+"F7.boolean.opBoolean","COPY",EDGE,{"derivedFrom":makeQuery(id+"F7.opExtrude","CAP_EDGE",EDGE,{"disambiguationData":[OSD([sQuery(id+"F6.wireOp",EDGE,"E8.0.9.0")])],"isStart":true})});
            var Q10;
            Q10=makeQuery(id+"F7.boolean.opBoolean","COPY",EDGE,{"derivedFrom":makeQuery(id+"F7.opExtrude","CAP_EDGE",EDGE,{"disambiguationData":[OSD([sQuery(id+"F6.wireOp",EDGE,"E8.0.10.0")])],"isStart":true})});
            var Q11;
            Q11=makeQuery(id+"F7.boolean.opBoolean","COPY",EDGE,{"derivedFrom":makeQuery(id+"F7.opExtrude","CAP_EDGE",EDGE,{"disambiguationData":[OSD([sQuery(id+"F6.wireOp",EDGE,"E8.0.11.0")])],"isStart":true})});
            var Q12;
            Q12=makeQuery(id+"F7.boolean.opBoolean","COPY",EDGE,{"derivedFrom":makeQuery(id+"F7.opExtrude","CAP_EDGE",EDGE,{"disambiguationData":[OSD([sQuery(id+"F6.wireOp",EDGE,"E8.0.12.0")])],"isStart":true})});
            var Q13;
            Q13=makeQuery(id+"F7.boolean.opBoolean","COPY",EDGE,{"derivedFrom":makeQuery(id+"F7.opExtrude","CAP_EDGE",EDGE,{"disambiguationData":[OSD([sQuery(id+"F6.wireOp",EDGE,"E8.0.13.0")])],"isStart":true})});
            var Q14;
            Q14=makeQuery(id+"F7.boolean.opBoolean","COPY",EDGE,{"derivedFrom":makeQuery(id+"F7.opExtrude","CAP_EDGE",EDGE,{"disambiguationData":[OSD([sQuery(id+"F6.wireOp",EDGE,"E8.0.14.0")])],"isStart":true})});
            var Q15;
            Q15=makeQuery(id+"F7.boolean.opBoolean","COPY",EDGE,{"derivedFrom":makeQuery(id+"F7.opExtrude","CAP_EDGE",EDGE,{"disambiguationData":[OSD([sQuery(id+"F6.wireOp",EDGE,"E9.0.0.15")])],"isStart":true})});
            var Q16;
            Q16=makeQuery(id+"F7.boolean.opBoolean","COPY",EDGE,{"derivedFrom":makeQuery(id+"F7.opExtrude","CAP_EDGE",EDGE,{"disambiguationData":[OSD([sQuery(id+"F6.wireOp",EDGE,"E9.0.0.16")])],"isStart":true})});
            var Q17;
            Q17=makeQuery(id+"F7.boolean.opBoolean","COPY",EDGE,{"derivedFrom":makeQuery(id+"F7.opExtrude","CAP_EDGE",EDGE,{"disambiguationData":[OSD([sQuery(id+"F6.wireOp",EDGE,"E9.0.0.17")])],"isStart":true})});
            var Q18;
            Q18=makeQuery(id+"F7.boolean.opBoolean","COPY",EDGE,{"derivedFrom":makeQuery(id+"F7.opExtrude","CAP_EDGE",EDGE,{"disambiguationData":[OSD([sQuery(id+"F6.wireOp",EDGE,"E9.0.0.18")])],"isStart":true})});
            var Q19;
            Q19=makeQuery(id+"F7.boolean.opBoolean","COPY",EDGE,{"derivedFrom":makeQuery(id+"F7.opExtrude","CAP_EDGE",EDGE,{"disambiguationData":[OSD([sQuery(id+"F6.wireOp",EDGE,"E9.0.0.19")])],"isStart":true})});
            var Q20;
            Q20=makeQuery(id+"F7.boolean.opBoolean","COPY",EDGE,{"derivedFrom":makeQuery(id+"F7.opExtrude","CAP_EDGE",EDGE,{"disambiguationData":[OSD([sQuery(id+"F6.wireOp",EDGE,"E9.0.7.19")])],"isStart":true})});
            var Q21;
            Q21=makeQuery(id+"F7.boolean.opBoolean","COPY",EDGE,{"derivedFrom":makeQuery(id+"F7.opExtrude","CAP_EDGE",EDGE,{"disambiguationData":[OSD([sQuery(id+"F6.wireOp",EDGE,"E9.0.7.18")])],"isStart":true})});
            var Q22;
            Q22=makeQuery(id+"F7.boolean.opBoolean","COPY",EDGE,{"derivedFrom":makeQuery(id+"F7.opExtrude","CAP_EDGE",EDGE,{"disambiguationData":[OSD([sQuery(id+"F6.wireOp",EDGE,"E9.0.7.17")])],"isStart":true})});
            var Q23;
            Q23=makeQuery(id+"F7.boolean.opBoolean","COPY",EDGE,{"derivedFrom":makeQuery(id+"F7.opExtrude","CAP_EDGE",EDGE,{"disambiguationData":[OSD([sQuery(id+"F6.wireOp",EDGE,"E9.0.7.16")])],"isStart":true})});
            var Q24;
            Q24=makeQuery(id+"F7.boolean.opBoolean","COPY",EDGE,{"derivedFrom":makeQuery(id+"F7.opExtrude","CAP_EDGE",EDGE,{"disambiguationData":[OSD([sQuery(id+"F6.wireOp",EDGE,"E9.0.7.15")])],"isStart":true})});
            var Q25;
            Q25=makeQuery(id+"F7.boolean.opBoolean","COPY",EDGE,{"derivedFrom":makeQuery(id+"F7.opExtrude","CAP_EDGE",EDGE,{"disambiguationData":[OSD([sQuery(id+"F6.wireOp",EDGE,"E9.0.6.19")])],"isStart":true})});
            var Q26;
            Q26=makeQuery(id+"F7.boolean.opBoolean","COPY",EDGE,{"derivedFrom":makeQuery(id+"F7.opExtrude","CAP_EDGE",EDGE,{"disambiguationData":[OSD([sQuery(id+"F6.wireOp",EDGE,"E9.0.6.18")])],"isStart":true})});
            var Q27;
            Q27=makeQuery(id+"F7.boolean.opBoolean","COPY",EDGE,{"derivedFrom":makeQuery(id+"F7.opExtrude","CAP_EDGE",EDGE,{"disambiguationData":[OSD([sQuery(id+"F6.wireOp",EDGE,"E9.0.6.17")])],"isStart":true})});
            var Q28;
            Q28=makeQuery(id+"F7.boolean.opBoolean","COPY",EDGE,{"derivedFrom":makeQuery(id+"F7.opExtrude","CAP_EDGE",EDGE,{"disambiguationData":[OSD([sQuery(id+"F6.wireOp",EDGE,"E9.0.6.16")])],"isStart":true})});
            var Q29;
            Q29=makeQuery(id+"F7.boolean.opBoolean","COPY",EDGE,{"derivedFrom":makeQuery(id+"F7.opExtrude","CAP_EDGE",EDGE,{"disambiguationData":[OSD([sQuery(id+"F6.wireOp",EDGE,"E9.0.6.15")])],"isStart":true})});
            var Q30;
            Q30=makeQuery(id+"F7.boolean.opBoolean","COPY",EDGE,{"derivedFrom":makeQuery(id+"F7.opExtrude","CAP_EDGE",EDGE,{"disambiguationData":[OSD([sQuery(id+"F6.wireOp",EDGE,"E9.0.5.19")])],"isStart":true})});
            var Q31;
            Q31=makeQuery(id+"F7.boolean.opBoolean","COPY",EDGE,{"derivedFrom":makeQuery(id+"F7.opExtrude","CAP_EDGE",EDGE,{"disambiguationData":[OSD([sQuery(id+"F6.wireOp",EDGE,"E9.0.5.18")])],"isStart":true})});
            var Q32;
            Q32=makeQuery(id+"F7.boolean.opBoolean","COPY",EDGE,{"derivedFrom":makeQuery(id+"F7.opExtrude","CAP_EDGE",EDGE,{"disambiguationData":[OSD([sQuery(id+"F6.wireOp",EDGE,"E9.0.5.17")])],"isStart":true})});
            var Q33;
            Q33=makeQuery(id+"F7.boolean.opBoolean","COPY",EDGE,{"derivedFrom":makeQuery(id+"F7.opExtrude","CAP_EDGE",EDGE,{"disambiguationData":[OSD([sQuery(id+"F6.wireOp",EDGE,"E9.0.5.16")])],"isStart":true})});
            var Q34;
            Q34=makeQuery(id+"F7.boolean.opBoolean","COPY",EDGE,{"derivedFrom":makeQuery(id+"F7.opExtrude","CAP_EDGE",EDGE,{"disambiguationData":[OSD([sQuery(id+"F6.wireOp",EDGE,"E9.0.5.15")])],"isStart":true})});
            var Q35;
            Q35=makeQuery(id+"F7.boolean.opBoolean","COPY",EDGE,{"derivedFrom":makeQuery(id+"F7.opExtrude","CAP_EDGE",EDGE,{"disambiguationData":[OSD([sQuery(id+"F6.wireOp",EDGE,"E9.0.4.19")])],"isStart":true})});
            var Q36;
            Q36=makeQuery(id+"F7.boolean.opBoolean","COPY",EDGE,{"derivedFrom":makeQuery(id+"F7.opExtrude","CAP_EDGE",EDGE,{"disambiguationData":[OSD([sQuery(id+"F6.wireOp",EDGE,"E9.0.4.18")])],"isStart":true})});
            var Q37;
            Q37=makeQuery(id+"F7.boolean.opBoolean","COPY",EDGE,{"derivedFrom":makeQuery(id+"F7.opExtrude","CAP_EDGE",EDGE,{"disambiguationData":[OSD([sQuery(id+"F6.wireOp",EDGE,"E9.0.4.17")])],"isStart":true})});
            var Q38;
            Q38=makeQuery(id+"F7.boolean.opBoolean","COPY",EDGE,{"derivedFrom":makeQuery(id+"F7.opExtrude","CAP_EDGE",EDGE,{"disambiguationData":[OSD([sQuery(id+"F6.wireOp",EDGE,"E9.0.4.16")])],"isStart":true})});
            var Q39;
            Q39=makeQuery(id+"F7.boolean.opBoolean","COPY",EDGE,{"derivedFrom":makeQuery(id+"F7.opExtrude","CAP_EDGE",EDGE,{"disambiguationData":[OSD([sQuery(id+"F6.wireOp",EDGE,"E9.0.4.15")])],"isStart":true})});
            var Q40;
            Q40=makeQuery(id+"F7.boolean.opBoolean","COPY",EDGE,{"derivedFrom":makeQuery(id+"F7.opExtrude","CAP_EDGE",EDGE,{"disambiguationData":[OSD([sQuery(id+"F6.wireOp",EDGE,"E9.0.3.19")])],"isStart":true})});
            var Q41;
            Q41=makeQuery(id+"F7.boolean.opBoolean","COPY",EDGE,{"derivedFrom":makeQuery(id+"F7.opExtrude","CAP_EDGE",EDGE,{"disambiguationData":[OSD([sQuery(id+"F6.wireOp",EDGE,"E9.0.3.18")])],"isStart":true})});
            var Q42;
            Q42=makeQuery(id+"F7.boolean.opBoolean","COPY",EDGE,{"derivedFrom":makeQuery(id+"F7.opExtrude","CAP_EDGE",EDGE,{"disambiguationData":[OSD([sQuery(id+"F6.wireOp",EDGE,"E9.0.3.17")])],"isStart":true})});
            var Q43;
            Q43=makeQuery(id+"F7.boolean.opBoolean","COPY",EDGE,{"derivedFrom":makeQuery(id+"F7.opExtrude","CAP_EDGE",EDGE,{"disambiguationData":[OSD([sQuery(id+"F6.wireOp",EDGE,"E9.0.3.16")])],"isStart":true})});
            var Q44;
            Q44=makeQuery(id+"F7.boolean.opBoolean","COPY",EDGE,{"derivedFrom":makeQuery(id+"F7.opExtrude","CAP_EDGE",EDGE,{"disambiguationData":[OSD([sQuery(id+"F6.wireOp",EDGE,"E9.0.3.15")])],"isStart":true})});
            var Q45;
            Q45=makeQuery(id+"F7.boolean.opBoolean","COPY",EDGE,{"derivedFrom":makeQuery(id+"F7.opExtrude","CAP_EDGE",EDGE,{"disambiguationData":[OSD([sQuery(id+"F6.wireOp",EDGE,"E9.0.2.19")])],"isStart":true})});
            var Q46;
            Q46=makeQuery(id+"F7.boolean.opBoolean","COPY",EDGE,{"derivedFrom":makeQuery(id+"F7.opExtrude","CAP_EDGE",EDGE,{"disambiguationData":[OSD([sQuery(id+"F6.wireOp",EDGE,"E9.0.2.18")])],"isStart":true})});
            var Q47;
            Q47=makeQuery(id+"F7.boolean.opBoolean","COPY",EDGE,{"derivedFrom":makeQuery(id+"F7.opExtrude","CAP_EDGE",EDGE,{"disambiguationData":[OSD([sQuery(id+"F6.wireOp",EDGE,"E9.0.2.17")])],"isStart":true})});
            var Q48;
            Q48=makeQuery(id+"F7.boolean.opBoolean","COPY",EDGE,{"derivedFrom":makeQuery(id+"F7.opExtrude","CAP_EDGE",EDGE,{"disambiguationData":[OSD([sQuery(id+"F6.wireOp",EDGE,"E9.0.2.16")])],"isStart":true})});
            var Q49;
            Q49=makeQuery(id+"F7.boolean.opBoolean","COPY",EDGE,{"derivedFrom":makeQuery(id+"F7.opExtrude","CAP_EDGE",EDGE,{"disambiguationData":[OSD([sQuery(id+"F6.wireOp",EDGE,"E9.0.2.15")])],"isStart":true})});
            var Q50;
            Q50=makeQuery(id+"F7.boolean.opBoolean","COPY",EDGE,{"derivedFrom":makeQuery(id+"F7.opExtrude","CAP_EDGE",EDGE,{"disambiguationData":[OSD([sQuery(id+"F6.wireOp",EDGE,"E9.0.1.19")])],"isStart":true})});
            var Q51;
            Q51=makeQuery(id+"F7.boolean.opBoolean","COPY",EDGE,{"derivedFrom":makeQuery(id+"F7.opExtrude","CAP_EDGE",EDGE,{"disambiguationData":[OSD([sQuery(id+"F6.wireOp",EDGE,"E9.0.1.18")])],"isStart":true})});
            var Q52;
            Q52=makeQuery(id+"F7.boolean.opBoolean","COPY",EDGE,{"derivedFrom":makeQuery(id+"F7.opExtrude","CAP_EDGE",EDGE,{"disambiguationData":[OSD([sQuery(id+"F6.wireOp",EDGE,"E9.0.1.17")])],"isStart":true})});
            var Q53;
            Q53=makeQuery(id+"F7.boolean.opBoolean","COPY",EDGE,{"derivedFrom":makeQuery(id+"F7.opExtrude","CAP_EDGE",EDGE,{"disambiguationData":[OSD([sQuery(id+"F6.wireOp",EDGE,"E9.0.1.16")])],"isStart":true})});
            var Q54;
            Q54=makeQuery(id+"F7.boolean.opBoolean","COPY",EDGE,{"derivedFrom":makeQuery(id+"F7.opExtrude","CAP_EDGE",EDGE,{"disambiguationData":[OSD([sQuery(id+"F6.wireOp",EDGE,"E9.0.1.15")])],"isStart":true})});
            var Q55;
            Q55=makeQuery(id+"F7.boolean.opBoolean","COPY",EDGE,{"derivedFrom":makeQuery(id+"F7.opExtrude","CAP_EDGE",EDGE,{"disambiguationData":[OSD([sQuery(id+"F6.wireOp",EDGE,"E8.8.14.0")])],"isStart":true})});
            var Q56;
            Q56=makeQuery(id+"F7.boolean.opBoolean","COPY",EDGE,{"derivedFrom":makeQuery(id+"F7.opExtrude","CAP_EDGE",EDGE,{"disambiguationData":[OSD([sQuery(id+"F6.wireOp",EDGE,"E8.8.13.0")])],"isStart":true})});
            var Q57;
            Q57=makeQuery(id+"F7.boolean.opBoolean","COPY",EDGE,{"derivedFrom":makeQuery(id+"F7.opExtrude","CAP_EDGE",EDGE,{"disambiguationData":[OSD([sQuery(id+"F6.wireOp",EDGE,"E8.8.12.0")])],"isStart":true})});
            var Q58;
            Q58=makeQuery(id+"F7.boolean.opBoolean","COPY",EDGE,{"derivedFrom":makeQuery(id+"F7.opExtrude","CAP_EDGE",EDGE,{"disambiguationData":[OSD([sQuery(id+"F6.wireOp",EDGE,"E8.8.11.0")])],"isStart":true})});
            var Q59;
            Q59=makeQuery(id+"F7.boolean.opBoolean","COPY",EDGE,{"derivedFrom":makeQuery(id+"F7.opExtrude","CAP_EDGE",EDGE,{"disambiguationData":[OSD([sQuery(id+"F6.wireOp",EDGE,"E8.8.10.0")])],"isStart":true})});
            var Q60;
            Q60=makeQuery(id+"F7.boolean.opBoolean","COPY",EDGE,{"derivedFrom":makeQuery(id+"F7.opExtrude","CAP_EDGE",EDGE,{"disambiguationData":[OSD([sQuery(id+"F6.wireOp",EDGE,"E8.8.9.0")])],"isStart":true})});
            var Q61;
            Q61=makeQuery(id+"F7.boolean.opBoolean","COPY",EDGE,{"derivedFrom":makeQuery(id+"F7.opExtrude","CAP_EDGE",EDGE,{"disambiguationData":[OSD([sQuery(id+"F6.wireOp",EDGE,"E8.8.8.0")])],"isStart":true})});
            var Q62;
            Q62=makeQuery(id+"F7.boolean.opBoolean","COPY",EDGE,{"derivedFrom":makeQuery(id+"F7.opExtrude","CAP_EDGE",EDGE,{"disambiguationData":[OSD([sQuery(id+"F6.wireOp",EDGE,"E8.8.7.0")])],"isStart":true})});
            var Q63;
            Q63=makeQuery(id+"F7.boolean.opBoolean","COPY",EDGE,{"derivedFrom":makeQuery(id+"F7.opExtrude","CAP_EDGE",EDGE,{"disambiguationData":[OSD([sQuery(id+"F6.wireOp",EDGE,"E8.8.6.0")])],"isStart":true})});
            var Q64;
            Q64=makeQuery(id+"F7.boolean.opBoolean","COPY",EDGE,{"derivedFrom":makeQuery(id+"F7.opExtrude","CAP_EDGE",EDGE,{"disambiguationData":[OSD([sQuery(id+"F6.wireOp",EDGE,"E8.8.5.0")])],"isStart":true})});
            var Q65;
            Q65=makeQuery(id+"F7.boolean.opBoolean","COPY",EDGE,{"derivedFrom":makeQuery(id+"F7.opExtrude","CAP_EDGE",EDGE,{"disambiguationData":[OSD([sQuery(id+"F6.wireOp",EDGE,"E8.8.4.0")])],"isStart":true})});
            var Q66;
            Q66=makeQuery(id+"F7.boolean.opBoolean","COPY",EDGE,{"derivedFrom":makeQuery(id+"F7.opExtrude","CAP_EDGE",EDGE,{"disambiguationData":[OSD([sQuery(id+"F6.wireOp",EDGE,"E8.8.3.0")])],"isStart":true})});
            var Q67;
            Q67=makeQuery(id+"F7.boolean.opBoolean","COPY",EDGE,{"derivedFrom":makeQuery(id+"F7.opExtrude","CAP_EDGE",EDGE,{"disambiguationData":[OSD([sQuery(id+"F6.wireOp",EDGE,"E8.8.2.0")])],"isStart":true})});
            var Q68;
            Q68=makeQuery(id+"F7.boolean.opBoolean","COPY",EDGE,{"derivedFrom":makeQuery(id+"F7.opExtrude","CAP_EDGE",EDGE,{"disambiguationData":[OSD([sQuery(id+"F6.wireOp",EDGE,"E8.8.1.0")])],"isStart":true})});
            var Q69;
            Q69=makeQuery(id+"F7.boolean.opBoolean","COPY",EDGE,{"derivedFrom":makeQuery(id+"F7.opExtrude","CAP_EDGE",EDGE,{"disambiguationData":[OSD([sQuery(id+"F6.wireOp",EDGE,"E8.8.0.0")])],"isStart":true})});
            var Q70;
            Q70=makeQuery(id+"F7.boolean.opBoolean","COPY",EDGE,{"derivedFrom":makeQuery(id+"F7.opExtrude","CAP_EDGE",EDGE,{"disambiguationData":[OSD([sQuery(id+"F6.wireOp",EDGE,"E8.7.14.0")])],"isStart":true})});
            var Q71;
            Q71=makeQuery(id+"F7.boolean.opBoolean","COPY",EDGE,{"derivedFrom":makeQuery(id+"F7.opExtrude","CAP_EDGE",EDGE,{"disambiguationData":[OSD([sQuery(id+"F6.wireOp",EDGE,"E8.7.13.0")])],"isStart":true})});
            var Q72;
            Q72=makeQuery(id+"F7.boolean.opBoolean","COPY",EDGE,{"derivedFrom":makeQuery(id+"F7.opExtrude","CAP_EDGE",EDGE,{"disambiguationData":[OSD([sQuery(id+"F6.wireOp",EDGE,"E8.7.12.0")])],"isStart":true})});
            var Q73;
            Q73=makeQuery(id+"F7.boolean.opBoolean","COPY",EDGE,{"derivedFrom":makeQuery(id+"F7.opExtrude","CAP_EDGE",EDGE,{"disambiguationData":[OSD([sQuery(id+"F6.wireOp",EDGE,"E8.7.11.0")])],"isStart":true})});
            var Q74;
            Q74=makeQuery(id+"F7.boolean.opBoolean","COPY",EDGE,{"derivedFrom":makeQuery(id+"F7.opExtrude","CAP_EDGE",EDGE,{"disambiguationData":[OSD([sQuery(id+"F6.wireOp",EDGE,"E8.7.10.0")])],"isStart":true})});
            var Q75;
            Q75=makeQuery(id+"F7.boolean.opBoolean","COPY",EDGE,{"derivedFrom":makeQuery(id+"F7.opExtrude","CAP_EDGE",EDGE,{"disambiguationData":[OSD([sQuery(id+"F6.wireOp",EDGE,"E8.7.9.0")])],"isStart":true})});
            var Q76;
            Q76=makeQuery(id+"F7.boolean.opBoolean","COPY",EDGE,{"derivedFrom":makeQuery(id+"F7.opExtrude","CAP_EDGE",EDGE,{"disambiguationData":[OSD([sQuery(id+"F6.wireOp",EDGE,"E8.7.8.0")])],"isStart":true})});
            var Q77;
            Q77=makeQuery(id+"F7.boolean.opBoolean","COPY",EDGE,{"derivedFrom":makeQuery(id+"F7.opExtrude","CAP_EDGE",EDGE,{"disambiguationData":[OSD([sQuery(id+"F6.wireOp",EDGE,"E8.7.7.0")])],"isStart":true})});
            var Q78;
            Q78=makeQuery(id+"F7.boolean.opBoolean","COPY",EDGE,{"derivedFrom":makeQuery(id+"F7.opExtrude","CAP_EDGE",EDGE,{"disambiguationData":[OSD([sQuery(id+"F6.wireOp",EDGE,"E8.7.6.0")])],"isStart":true})});
            var Q79;
            Q79=makeQuery(id+"F7.boolean.opBoolean","COPY",EDGE,{"derivedFrom":makeQuery(id+"F7.opExtrude","CAP_EDGE",EDGE,{"disambiguationData":[OSD([sQuery(id+"F6.wireOp",EDGE,"E8.7.5.0")])],"isStart":true})});
            var Q80;
            Q80=makeQuery(id+"F7.boolean.opBoolean","COPY",EDGE,{"derivedFrom":makeQuery(id+"F7.opExtrude","CAP_EDGE",EDGE,{"disambiguationData":[OSD([sQuery(id+"F6.wireOp",EDGE,"E8.7.4.0")])],"isStart":true})});
            var Q81;
            Q81=makeQuery(id+"F7.boolean.opBoolean","COPY",EDGE,{"derivedFrom":makeQuery(id+"F7.opExtrude","CAP_EDGE",EDGE,{"disambiguationData":[OSD([sQuery(id+"F6.wireOp",EDGE,"E8.7.3.0")])],"isStart":true})});
            var Q82;
            Q82=makeQuery(id+"F7.boolean.opBoolean","COPY",EDGE,{"derivedFrom":makeQuery(id+"F7.opExtrude","CAP_EDGE",EDGE,{"disambiguationData":[OSD([sQuery(id+"F6.wireOp",EDGE,"E8.7.2.0")])],"isStart":true})});
            var Q83;
            Q83=makeQuery(id+"F7.boolean.opBoolean","COPY",EDGE,{"derivedFrom":makeQuery(id+"F7.opExtrude","CAP_EDGE",EDGE,{"disambiguationData":[OSD([sQuery(id+"F6.wireOp",EDGE,"E8.7.1.0")])],"isStart":true})});
            var Q84;
            Q84=makeQuery(id+"F7.boolean.opBoolean","COPY",EDGE,{"derivedFrom":makeQuery(id+"F7.opExtrude","CAP_EDGE",EDGE,{"disambiguationData":[OSD([sQuery(id+"F6.wireOp",EDGE,"E8.7.0.0")])],"isStart":true})});
            var Q85;
            Q85=makeQuery(id+"F7.boolean.opBoolean","COPY",EDGE,{"derivedFrom":makeQuery(id+"F7.opExtrude","CAP_EDGE",EDGE,{"disambiguationData":[OSD([sQuery(id+"F6.wireOp",EDGE,"E8.6.14.0")])],"isStart":true})});
            var Q86;
            Q86=makeQuery(id+"F7.boolean.opBoolean","COPY",EDGE,{"derivedFrom":makeQuery(id+"F7.opExtrude","CAP_EDGE",EDGE,{"disambiguationData":[OSD([sQuery(id+"F6.wireOp",EDGE,"E8.6.13.0")])],"isStart":true})});
            var Q87;
            Q87=makeQuery(id+"F7.boolean.opBoolean","COPY",EDGE,{"derivedFrom":makeQuery(id+"F7.opExtrude","CAP_EDGE",EDGE,{"disambiguationData":[OSD([sQuery(id+"F6.wireOp",EDGE,"E8.6.12.0")])],"isStart":true})});
            var Q88;
            Q88=makeQuery(id+"F7.boolean.opBoolean","COPY",EDGE,{"derivedFrom":makeQuery(id+"F7.opExtrude","CAP_EDGE",EDGE,{"disambiguationData":[OSD([sQuery(id+"F6.wireOp",EDGE,"E8.6.11.0")])],"isStart":true})});
            var Q89;
            Q89=makeQuery(id+"F7.boolean.opBoolean","COPY",EDGE,{"derivedFrom":makeQuery(id+"F7.opExtrude","CAP_EDGE",EDGE,{"disambiguationData":[OSD([sQuery(id+"F6.wireOp",EDGE,"E8.6.10.0")])],"isStart":true})});
            var Q90;
            Q90=makeQuery(id+"F7.boolean.opBoolean","COPY",EDGE,{"derivedFrom":makeQuery(id+"F7.opExtrude","CAP_EDGE",EDGE,{"disambiguationData":[OSD([sQuery(id+"F6.wireOp",EDGE,"E8.6.9.0")])],"isStart":true})});
            var Q91;
            Q91=makeQuery(id+"F7.boolean.opBoolean","COPY",EDGE,{"derivedFrom":makeQuery(id+"F7.opExtrude","CAP_EDGE",EDGE,{"disambiguationData":[OSD([sQuery(id+"F6.wireOp",EDGE,"E8.6.8.0")])],"isStart":true})});
            var Q92;
            Q92=makeQuery(id+"F7.boolean.opBoolean","COPY",EDGE,{"derivedFrom":makeQuery(id+"F7.opExtrude","CAP_EDGE",EDGE,{"disambiguationData":[OSD([sQuery(id+"F6.wireOp",EDGE,"E8.6.7.0")])],"isStart":true})});
            var Q93;
            Q93=makeQuery(id+"F7.boolean.opBoolean","COPY",EDGE,{"derivedFrom":makeQuery(id+"F7.opExtrude","CAP_EDGE",EDGE,{"disambiguationData":[OSD([sQuery(id+"F6.wireOp",EDGE,"E8.6.6.0")])],"isStart":true})});
            var Q94;
            Q94=makeQuery(id+"F7.boolean.opBoolean","COPY",EDGE,{"derivedFrom":makeQuery(id+"F7.opExtrude","CAP_EDGE",EDGE,{"disambiguationData":[OSD([sQuery(id+"F6.wireOp",EDGE,"E8.6.5.0")])],"isStart":true})});
            var Q95;
            Q95=makeQuery(id+"F7.boolean.opBoolean","COPY",EDGE,{"derivedFrom":makeQuery(id+"F7.opExtrude","CAP_EDGE",EDGE,{"disambiguationData":[OSD([sQuery(id+"F6.wireOp",EDGE,"E8.6.4.0")])],"isStart":true})});
            var Q96;
            Q96=makeQuery(id+"F7.boolean.opBoolean","COPY",EDGE,{"derivedFrom":makeQuery(id+"F7.opExtrude","CAP_EDGE",EDGE,{"disambiguationData":[OSD([sQuery(id+"F6.wireOp",EDGE,"E8.6.3.0")])],"isStart":true})});
            var Q97;
            Q97=makeQuery(id+"F7.boolean.opBoolean","COPY",EDGE,{"derivedFrom":makeQuery(id+"F7.opExtrude","CAP_EDGE",EDGE,{"disambiguationData":[OSD([sQuery(id+"F6.wireOp",EDGE,"E8.6.2.0")])],"isStart":true})});
            var Q98;
            Q98=makeQuery(id+"F7.boolean.opBoolean","COPY",EDGE,{"derivedFrom":makeQuery(id+"F7.opExtrude","CAP_EDGE",EDGE,{"disambiguationData":[OSD([sQuery(id+"F6.wireOp",EDGE,"E8.6.1.0")])],"isStart":true})});
            var Q99;
            Q99=makeQuery(id+"F7.boolean.opBoolean","COPY",EDGE,{"derivedFrom":makeQuery(id+"F7.opExtrude","CAP_EDGE",EDGE,{"disambiguationData":[OSD([sQuery(id+"F6.wireOp",EDGE,"E8.6.0.0")])],"isStart":true})});
            var Q100;
            Q100=makeQuery(id+"F7.boolean.opBoolean","COPY",EDGE,{"derivedFrom":makeQuery(id+"F7.opExtrude","CAP_EDGE",EDGE,{"disambiguationData":[OSD([sQuery(id+"F6.wireOp",EDGE,"E8.5.14.0")])],"isStart":true})});
            var Q101;
            Q101=makeQuery(id+"F7.boolean.opBoolean","COPY",EDGE,{"derivedFrom":makeQuery(id+"F7.opExtrude","CAP_EDGE",EDGE,{"disambiguationData":[OSD([sQuery(id+"F6.wireOp",EDGE,"E8.5.13.0")])],"isStart":true})});
            var Q102;
            Q102=makeQuery(id+"F7.boolean.opBoolean","COPY",EDGE,{"derivedFrom":makeQuery(id+"F7.opExtrude","CAP_EDGE",EDGE,{"disambiguationData":[OSD([sQuery(id+"F6.wireOp",EDGE,"E8.5.12.0")])],"isStart":true})});
            var Q103;
            Q103=makeQuery(id+"F7.boolean.opBoolean","COPY",EDGE,{"derivedFrom":makeQuery(id+"F7.opExtrude","CAP_EDGE",EDGE,{"disambiguationData":[OSD([sQuery(id+"F6.wireOp",EDGE,"E8.5.11.0")])],"isStart":true})});
            var Q104;
            Q104=makeQuery(id+"F7.boolean.opBoolean","COPY",EDGE,{"derivedFrom":makeQuery(id+"F7.opExtrude","CAP_EDGE",EDGE,{"disambiguationData":[OSD([sQuery(id+"F6.wireOp",EDGE,"E8.5.10.0")])],"isStart":true})});
            var Q105;
            Q105=makeQuery(id+"F7.boolean.opBoolean","COPY",EDGE,{"derivedFrom":makeQuery(id+"F7.opExtrude","CAP_EDGE",EDGE,{"disambiguationData":[OSD([sQuery(id+"F6.wireOp",EDGE,"E8.5.9.0")])],"isStart":true})});
            var Q106;
            Q106=makeQuery(id+"F7.boolean.opBoolean","COPY",EDGE,{"derivedFrom":makeQuery(id+"F7.opExtrude","CAP_EDGE",EDGE,{"disambiguationData":[OSD([sQuery(id+"F6.wireOp",EDGE,"E8.5.8.0")])],"isStart":true})});
            var Q107;
            Q107=makeQuery(id+"F7.boolean.opBoolean","COPY",EDGE,{"derivedFrom":makeQuery(id+"F7.opExtrude","CAP_EDGE",EDGE,{"disambiguationData":[OSD([sQuery(id+"F6.wireOp",EDGE,"E8.5.7.0")])],"isStart":true})});
            var Q108;
            Q108=makeQuery(id+"F7.boolean.opBoolean","COPY",EDGE,{"derivedFrom":makeQuery(id+"F7.opExtrude","CAP_EDGE",EDGE,{"disambiguationData":[OSD([sQuery(id+"F6.wireOp",EDGE,"E8.5.6.0")])],"isStart":true})});
            var Q109;
            Q109=makeQuery(id+"F7.boolean.opBoolean","COPY",EDGE,{"derivedFrom":makeQuery(id+"F7.opExtrude","CAP_EDGE",EDGE,{"disambiguationData":[OSD([sQuery(id+"F6.wireOp",EDGE,"E8.5.5.0")])],"isStart":true})});
            var Q110;
            Q110=makeQuery(id+"F7.boolean.opBoolean","COPY",EDGE,{"derivedFrom":makeQuery(id+"F7.opExtrude","CAP_EDGE",EDGE,{"disambiguationData":[OSD([sQuery(id+"F6.wireOp",EDGE,"E8.5.4.0")])],"isStart":true})});
            var Q111;
            Q111=makeQuery(id+"F7.boolean.opBoolean","COPY",EDGE,{"derivedFrom":makeQuery(id+"F7.opExtrude","CAP_EDGE",EDGE,{"disambiguationData":[OSD([sQuery(id+"F6.wireOp",EDGE,"E8.5.3.0")])],"isStart":true})});
            var Q112;
            Q112=makeQuery(id+"F7.boolean.opBoolean","COPY",EDGE,{"derivedFrom":makeQuery(id+"F7.opExtrude","CAP_EDGE",EDGE,{"disambiguationData":[OSD([sQuery(id+"F6.wireOp",EDGE,"E8.5.2.0")])],"isStart":true})});
            var Q113;
            Q113=makeQuery(id+"F7.boolean.opBoolean","COPY",EDGE,{"derivedFrom":makeQuery(id+"F7.opExtrude","CAP_EDGE",EDGE,{"disambiguationData":[OSD([sQuery(id+"F6.wireOp",EDGE,"E8.5.1.0")])],"isStart":true})});
            var Q114;
            Q114=makeQuery(id+"F7.boolean.opBoolean","COPY",EDGE,{"derivedFrom":makeQuery(id+"F7.opExtrude","CAP_EDGE",EDGE,{"disambiguationData":[OSD([sQuery(id+"F6.wireOp",EDGE,"E8.5.0.0")])],"isStart":true})});
            var Q115;
            Q115=makeQuery(id+"F7.boolean.opBoolean","COPY",EDGE,{"derivedFrom":makeQuery(id+"F7.opExtrude","CAP_EDGE",EDGE,{"disambiguationData":[OSD([sQuery(id+"F6.wireOp",EDGE,"E8.4.14.0")])],"isStart":true})});
            var Q116;
            Q116=makeQuery(id+"F7.boolean.opBoolean","COPY",EDGE,{"derivedFrom":makeQuery(id+"F7.opExtrude","CAP_EDGE",EDGE,{"disambiguationData":[OSD([sQuery(id+"F6.wireOp",EDGE,"E8.4.13.0")])],"isStart":true})});
            var Q117;
            Q117=makeQuery(id+"F7.boolean.opBoolean","COPY",EDGE,{"derivedFrom":makeQuery(id+"F7.opExtrude","CAP_EDGE",EDGE,{"disambiguationData":[OSD([sQuery(id+"F6.wireOp",EDGE,"E8.4.12.0")])],"isStart":true})});
            var Q118;
            Q118=makeQuery(id+"F7.boolean.opBoolean","COPY",EDGE,{"derivedFrom":makeQuery(id+"F7.opExtrude","CAP_EDGE",EDGE,{"disambiguationData":[OSD([sQuery(id+"F6.wireOp",EDGE,"E8.4.11.0")])],"isStart":true})});
            var Q119;
            Q119=makeQuery(id+"F7.boolean.opBoolean","COPY",EDGE,{"derivedFrom":makeQuery(id+"F7.opExtrude","CAP_EDGE",EDGE,{"disambiguationData":[OSD([sQuery(id+"F6.wireOp",EDGE,"E8.4.10.0")])],"isStart":true})});
            var Q120;
            Q120=makeQuery(id+"F7.boolean.opBoolean","COPY",EDGE,{"derivedFrom":makeQuery(id+"F7.opExtrude","CAP_EDGE",EDGE,{"disambiguationData":[OSD([sQuery(id+"F6.wireOp",EDGE,"E8.4.9.0")])],"isStart":true})});
            var Q121;
            Q121=makeQuery(id+"F7.boolean.opBoolean","COPY",EDGE,{"derivedFrom":makeQuery(id+"F7.opExtrude","CAP_EDGE",EDGE,{"disambiguationData":[OSD([sQuery(id+"F6.wireOp",EDGE,"E8.4.8.0")])],"isStart":true})});
            var Q122;
            Q122=makeQuery(id+"F7.boolean.opBoolean","COPY",EDGE,{"derivedFrom":makeQuery(id+"F7.opExtrude","CAP_EDGE",EDGE,{"disambiguationData":[OSD([sQuery(id+"F6.wireOp",EDGE,"E8.4.7.0")])],"isStart":true})});
            var Q123;
            Q123=makeQuery(id+"F7.boolean.opBoolean","COPY",EDGE,{"derivedFrom":makeQuery(id+"F7.opExtrude","CAP_EDGE",EDGE,{"disambiguationData":[OSD([sQuery(id+"F6.wireOp",EDGE,"E8.4.6.0")])],"isStart":true})});
            var Q124;
            Q124=makeQuery(id+"F7.boolean.opBoolean","COPY",EDGE,{"derivedFrom":makeQuery(id+"F7.opExtrude","CAP_EDGE",EDGE,{"disambiguationData":[OSD([sQuery(id+"F6.wireOp",EDGE,"E8.4.5.0")])],"isStart":true})});
            var Q125;
            Q125=makeQuery(id+"F7.boolean.opBoolean","COPY",EDGE,{"derivedFrom":makeQuery(id+"F7.opExtrude","CAP_EDGE",EDGE,{"disambiguationData":[OSD([sQuery(id+"F6.wireOp",EDGE,"E8.4.4.0")])],"isStart":true})});
            var Q126;
            Q126=makeQuery(id+"F7.boolean.opBoolean","COPY",EDGE,{"derivedFrom":makeQuery(id+"F7.opExtrude","CAP_EDGE",EDGE,{"disambiguationData":[OSD([sQuery(id+"F6.wireOp",EDGE,"E8.4.3.0")])],"isStart":true})});
            var Q127;
            Q127=makeQuery(id+"F7.boolean.opBoolean","COPY",EDGE,{"derivedFrom":makeQuery(id+"F7.opExtrude","CAP_EDGE",EDGE,{"disambiguationData":[OSD([sQuery(id+"F6.wireOp",EDGE,"E8.4.2.0")])],"isStart":true})});
            var Q128;
            Q128=makeQuery(id+"F7.boolean.opBoolean","COPY",EDGE,{"derivedFrom":makeQuery(id+"F7.opExtrude","CAP_EDGE",EDGE,{"disambiguationData":[OSD([sQuery(id+"F6.wireOp",EDGE,"E8.4.1.0")])],"isStart":true})});
            var Q129;
            Q129=makeQuery(id+"F7.boolean.opBoolean","COPY",EDGE,{"derivedFrom":makeQuery(id+"F7.opExtrude","CAP_EDGE",EDGE,{"disambiguationData":[OSD([sQuery(id+"F6.wireOp",EDGE,"E8.4.0.0")])],"isStart":true})});
            var Q130;
            Q130=makeQuery(id+"F7.boolean.opBoolean","COPY",EDGE,{"derivedFrom":makeQuery(id+"F7.opExtrude","CAP_EDGE",EDGE,{"disambiguationData":[OSD([sQuery(id+"F6.wireOp",EDGE,"E8.3.14.0")])],"isStart":true})});
            var Q131;
            Q131=makeQuery(id+"F7.boolean.opBoolean","COPY",EDGE,{"derivedFrom":makeQuery(id+"F7.opExtrude","CAP_EDGE",EDGE,{"disambiguationData":[OSD([sQuery(id+"F6.wireOp",EDGE,"E8.3.13.0")])],"isStart":true})});
            var Q132;
            Q132=makeQuery(id+"F7.boolean.opBoolean","COPY",EDGE,{"derivedFrom":makeQuery(id+"F7.opExtrude","CAP_EDGE",EDGE,{"disambiguationData":[OSD([sQuery(id+"F6.wireOp",EDGE,"E8.3.12.0")])],"isStart":true})});
            var Q133;
            Q133=makeQuery(id+"F7.boolean.opBoolean","COPY",EDGE,{"derivedFrom":makeQuery(id+"F7.opExtrude","CAP_EDGE",EDGE,{"disambiguationData":[OSD([sQuery(id+"F6.wireOp",EDGE,"E8.3.11.0")])],"isStart":true})});
            var Q134;
            Q134=makeQuery(id+"F7.boolean.opBoolean","COPY",EDGE,{"derivedFrom":makeQuery(id+"F7.opExtrude","CAP_EDGE",EDGE,{"disambiguationData":[OSD([sQuery(id+"F6.wireOp",EDGE,"E8.3.10.0")])],"isStart":true})});
            var Q135;
            Q135=makeQuery(id+"F7.boolean.opBoolean","COPY",EDGE,{"derivedFrom":makeQuery(id+"F7.opExtrude","CAP_EDGE",EDGE,{"disambiguationData":[OSD([sQuery(id+"F6.wireOp",EDGE,"E8.3.9.0")])],"isStart":true})});
            var Q136;
            Q136=makeQuery(id+"F7.boolean.opBoolean","COPY",EDGE,{"derivedFrom":makeQuery(id+"F7.opExtrude","CAP_EDGE",EDGE,{"disambiguationData":[OSD([sQuery(id+"F6.wireOp",EDGE,"E8.3.8.0")])],"isStart":true})});
            var Q137;
            Q137=makeQuery(id+"F7.boolean.opBoolean","COPY",EDGE,{"derivedFrom":makeQuery(id+"F7.opExtrude","CAP_EDGE",EDGE,{"disambiguationData":[OSD([sQuery(id+"F6.wireOp",EDGE,"E8.3.7.0")])],"isStart":true})});
            var Q138;
            Q138=makeQuery(id+"F7.boolean.opBoolean","COPY",EDGE,{"derivedFrom":makeQuery(id+"F7.opExtrude","CAP_EDGE",EDGE,{"disambiguationData":[OSD([sQuery(id+"F6.wireOp",EDGE,"E8.3.6.0")])],"isStart":true})});
            var Q139;
            Q139=makeQuery(id+"F7.boolean.opBoolean","COPY",EDGE,{"derivedFrom":makeQuery(id+"F7.opExtrude","CAP_EDGE",EDGE,{"disambiguationData":[OSD([sQuery(id+"F6.wireOp",EDGE,"E8.3.5.0")])],"isStart":true})});
            var Q140;
            Q140=makeQuery(id+"F7.boolean.opBoolean","COPY",EDGE,{"derivedFrom":makeQuery(id+"F7.opExtrude","CAP_EDGE",EDGE,{"disambiguationData":[OSD([sQuery(id+"F6.wireOp",EDGE,"E8.3.4.0")])],"isStart":true})});
            var Q141;
            Q141=makeQuery(id+"F7.boolean.opBoolean","COPY",EDGE,{"derivedFrom":makeQuery(id+"F7.opExtrude","CAP_EDGE",EDGE,{"disambiguationData":[OSD([sQuery(id+"F6.wireOp",EDGE,"E8.3.3.0")])],"isStart":true})});
            var Q142;
            Q142=makeQuery(id+"F7.boolean.opBoolean","COPY",EDGE,{"derivedFrom":makeQuery(id+"F7.opExtrude","CAP_EDGE",EDGE,{"disambiguationData":[OSD([sQuery(id+"F6.wireOp",EDGE,"E8.3.2.0")])],"isStart":true})});
            var Q143;
            Q143=makeQuery(id+"F7.boolean.opBoolean","COPY",EDGE,{"derivedFrom":makeQuery(id+"F7.opExtrude","CAP_EDGE",EDGE,{"disambiguationData":[OSD([sQuery(id+"F6.wireOp",EDGE,"E8.3.1.0")])],"isStart":true})});
            var Q144;
            Q144=makeQuery(id+"F7.boolean.opBoolean","COPY",EDGE,{"derivedFrom":makeQuery(id+"F7.opExtrude","CAP_EDGE",EDGE,{"disambiguationData":[OSD([sQuery(id+"F6.wireOp",EDGE,"E8.3.0.0")])],"isStart":true})});
            var Q145;
            Q145=makeQuery(id+"F7.boolean.opBoolean","COPY",EDGE,{"derivedFrom":makeQuery(id+"F7.opExtrude","CAP_EDGE",EDGE,{"disambiguationData":[OSD([sQuery(id+"F6.wireOp",EDGE,"E8.2.14.0")])],"isStart":true})});
            var Q146;
            Q146=makeQuery(id+"F7.boolean.opBoolean","COPY",EDGE,{"derivedFrom":makeQuery(id+"F7.opExtrude","CAP_EDGE",EDGE,{"disambiguationData":[OSD([sQuery(id+"F6.wireOp",EDGE,"E8.2.13.0")])],"isStart":true})});
            var Q147;
            Q147=makeQuery(id+"F7.boolean.opBoolean","COPY",EDGE,{"derivedFrom":makeQuery(id+"F7.opExtrude","CAP_EDGE",EDGE,{"disambiguationData":[OSD([sQuery(id+"F6.wireOp",EDGE,"E8.2.12.0")])],"isStart":true})});
            var Q148;
            Q148=makeQuery(id+"F7.boolean.opBoolean","COPY",EDGE,{"derivedFrom":makeQuery(id+"F7.opExtrude","CAP_EDGE",EDGE,{"disambiguationData":[OSD([sQuery(id+"F6.wireOp",EDGE,"E8.2.11.0")])],"isStart":true})});
            var Q149;
            Q149=makeQuery(id+"F7.boolean.opBoolean","COPY",EDGE,{"derivedFrom":makeQuery(id+"F7.opExtrude","CAP_EDGE",EDGE,{"disambiguationData":[OSD([sQuery(id+"F6.wireOp",EDGE,"E8.2.10.0")])],"isStart":true})});
            var Q150;
            Q150=makeQuery(id+"F7.boolean.opBoolean","COPY",EDGE,{"derivedFrom":makeQuery(id+"F7.opExtrude","CAP_EDGE",EDGE,{"disambiguationData":[OSD([sQuery(id+"F6.wireOp",EDGE,"E8.2.9.0")])],"isStart":true})});
            var Q151;
            Q151=makeQuery(id+"F7.boolean.opBoolean","COPY",EDGE,{"derivedFrom":makeQuery(id+"F7.opExtrude","CAP_EDGE",EDGE,{"disambiguationData":[OSD([sQuery(id+"F6.wireOp",EDGE,"E8.2.8.0")])],"isStart":true})});
            var Q152;
            Q152=makeQuery(id+"F7.boolean.opBoolean","COPY",EDGE,{"derivedFrom":makeQuery(id+"F7.opExtrude","CAP_EDGE",EDGE,{"disambiguationData":[OSD([sQuery(id+"F6.wireOp",EDGE,"E8.2.7.0")])],"isStart":true})});
            var Q153;
            Q153=makeQuery(id+"F7.boolean.opBoolean","COPY",EDGE,{"derivedFrom":makeQuery(id+"F7.opExtrude","CAP_EDGE",EDGE,{"disambiguationData":[OSD([sQuery(id+"F6.wireOp",EDGE,"E8.2.6.0")])],"isStart":true})});
            var Q154;
            Q154=makeQuery(id+"F7.boolean.opBoolean","COPY",EDGE,{"derivedFrom":makeQuery(id+"F7.opExtrude","CAP_EDGE",EDGE,{"disambiguationData":[OSD([sQuery(id+"F6.wireOp",EDGE,"E8.2.5.0")])],"isStart":true})});
            var Q155;
            Q155=makeQuery(id+"F7.boolean.opBoolean","COPY",EDGE,{"derivedFrom":makeQuery(id+"F7.opExtrude","CAP_EDGE",EDGE,{"disambiguationData":[OSD([sQuery(id+"F6.wireOp",EDGE,"E8.2.4.0")])],"isStart":true})});
            var Q156;
            Q156=makeQuery(id+"F7.boolean.opBoolean","COPY",EDGE,{"derivedFrom":makeQuery(id+"F7.opExtrude","CAP_EDGE",EDGE,{"disambiguationData":[OSD([sQuery(id+"F6.wireOp",EDGE,"E8.2.3.0")])],"isStart":true})});
            var Q157;
            Q157=makeQuery(id+"F7.boolean.opBoolean","COPY",EDGE,{"derivedFrom":makeQuery(id+"F7.opExtrude","CAP_EDGE",EDGE,{"disambiguationData":[OSD([sQuery(id+"F6.wireOp",EDGE,"E8.2.2.0")])],"isStart":true})});
            var Q158;
            Q158=makeQuery(id+"F7.boolean.opBoolean","COPY",EDGE,{"derivedFrom":makeQuery(id+"F7.opExtrude","CAP_EDGE",EDGE,{"disambiguationData":[OSD([sQuery(id+"F6.wireOp",EDGE,"E8.2.1.0")])],"isStart":true})});
            var Q159;
            Q159=makeQuery(id+"F7.boolean.opBoolean","COPY",EDGE,{"derivedFrom":makeQuery(id+"F7.opExtrude","CAP_EDGE",EDGE,{"disambiguationData":[OSD([sQuery(id+"F6.wireOp",EDGE,"E8.2.0.0")])],"isStart":true})});
            var Q160;
            Q160=makeQuery(id+"F7.boolean.opBoolean","COPY",EDGE,{"derivedFrom":makeQuery(id+"F7.opExtrude","CAP_EDGE",EDGE,{"disambiguationData":[OSD([sQuery(id+"F6.wireOp",EDGE,"E8.1.14.0")])],"isStart":true})});
            var Q161;
            Q161=makeQuery(id+"F7.boolean.opBoolean","COPY",EDGE,{"derivedFrom":makeQuery(id+"F7.opExtrude","CAP_EDGE",EDGE,{"disambiguationData":[OSD([sQuery(id+"F6.wireOp",EDGE,"E8.1.13.0")])],"isStart":true})});
            var Q162;
            Q162=makeQuery(id+"F7.boolean.opBoolean","COPY",EDGE,{"derivedFrom":makeQuery(id+"F7.opExtrude","CAP_EDGE",EDGE,{"disambiguationData":[OSD([sQuery(id+"F6.wireOp",EDGE,"E8.1.12.0")])],"isStart":true})});
            var Q163;
            Q163=makeQuery(id+"F7.boolean.opBoolean","COPY",EDGE,{"derivedFrom":makeQuery(id+"F7.opExtrude","CAP_EDGE",EDGE,{"disambiguationData":[OSD([sQuery(id+"F6.wireOp",EDGE,"E8.1.11.0")])],"isStart":true})});
            var Q164;
            Q164=makeQuery(id+"F7.boolean.opBoolean","COPY",EDGE,{"derivedFrom":makeQuery(id+"F7.opExtrude","CAP_EDGE",EDGE,{"disambiguationData":[OSD([sQuery(id+"F6.wireOp",EDGE,"E8.1.10.0")])],"isStart":true})});
            var Q165;
            Q165=makeQuery(id+"F7.boolean.opBoolean","COPY",EDGE,{"derivedFrom":makeQuery(id+"F7.opExtrude","CAP_EDGE",EDGE,{"disambiguationData":[OSD([sQuery(id+"F6.wireOp",EDGE,"E8.1.9.0")])],"isStart":true})});
            var Q166;
            Q166=makeQuery(id+"F7.boolean.opBoolean","COPY",EDGE,{"derivedFrom":makeQuery(id+"F7.opExtrude","CAP_EDGE",EDGE,{"disambiguationData":[OSD([sQuery(id+"F6.wireOp",EDGE,"E8.1.8.0")])],"isStart":true})});
            var Q167;
            Q167=makeQuery(id+"F7.boolean.opBoolean","COPY",EDGE,{"derivedFrom":makeQuery(id+"F7.opExtrude","CAP_EDGE",EDGE,{"disambiguationData":[OSD([sQuery(id+"F6.wireOp",EDGE,"E8.1.7.0")])],"isStart":true})});
            var Q168;
            Q168=makeQuery(id+"F7.boolean.opBoolean","COPY",EDGE,{"derivedFrom":makeQuery(id+"F7.opExtrude","CAP_EDGE",EDGE,{"disambiguationData":[OSD([sQuery(id+"F6.wireOp",EDGE,"E8.1.6.0")])],"isStart":true})});
            var Q169;
            Q169=makeQuery(id+"F7.boolean.opBoolean","COPY",EDGE,{"derivedFrom":makeQuery(id+"F7.opExtrude","CAP_EDGE",EDGE,{"disambiguationData":[OSD([sQuery(id+"F6.wireOp",EDGE,"E8.1.5.0")])],"isStart":true})});
            var Q170;
            Q170=makeQuery(id+"F7.boolean.opBoolean","COPY",EDGE,{"derivedFrom":makeQuery(id+"F7.opExtrude","CAP_EDGE",EDGE,{"disambiguationData":[OSD([sQuery(id+"F6.wireOp",EDGE,"E8.1.4.0")])],"isStart":true})});
            var Q171;
            Q171=makeQuery(id+"F7.boolean.opBoolean","COPY",EDGE,{"derivedFrom":makeQuery(id+"F7.opExtrude","CAP_EDGE",EDGE,{"disambiguationData":[OSD([sQuery(id+"F6.wireOp",EDGE,"E8.1.3.0")])],"isStart":true})});
            var Q172;
            Q172=makeQuery(id+"F7.boolean.opBoolean","COPY",EDGE,{"derivedFrom":makeQuery(id+"F7.opExtrude","CAP_EDGE",EDGE,{"disambiguationData":[OSD([sQuery(id+"F6.wireOp",EDGE,"E8.1.2.0")])],"isStart":true})});
            var Q173;
            Q173=makeQuery(id+"F7.boolean.opBoolean","COPY",EDGE,{"derivedFrom":makeQuery(id+"F7.opExtrude","CAP_EDGE",EDGE,{"disambiguationData":[OSD([sQuery(id+"F6.wireOp",EDGE,"E8.1.1.0")])],"isStart":true})});
            var Q174;
            Q174=makeQuery(id+"F7.boolean.opBoolean","COPY",EDGE,{"derivedFrom":makeQuery(id+"F7.opExtrude","CAP_EDGE",EDGE,{"disambiguationData":[OSD([sQuery(id+"F6.wireOp",EDGE,"E8.1.0.0")])],"isStart":true})});
            var Q175;
            Q175=makeQuery(id+"F7.boolean.opBoolean","COPY",EDGE,{"derivedFrom":makeQuery(id+"F7.opExtrude","CAP_EDGE",EDGE,{"disambiguationData":[OSD([sQuery(id+"F6.wireOp",EDGE,"E9.0.8.19")])],"isStart":true})});
            var Q176;
            Q176=makeQuery(id+"F7.boolean.opBoolean","COPY",EDGE,{"derivedFrom":makeQuery(id+"F7.opExtrude","CAP_EDGE",EDGE,{"disambiguationData":[OSD([sQuery(id+"F6.wireOp",EDGE,"E9.0.8.18")])],"isStart":true})});
            var Q177;
            Q177=makeQuery(id+"F7.boolean.opBoolean","COPY",EDGE,{"derivedFrom":makeQuery(id+"F7.opExtrude","CAP_EDGE",EDGE,{"disambiguationData":[OSD([sQuery(id+"F6.wireOp",EDGE,"E9.0.8.17")])],"isStart":true})});
            var Q178;
            Q178=makeQuery(id+"F7.boolean.opBoolean","COPY",EDGE,{"derivedFrom":makeQuery(id+"F7.opExtrude","CAP_EDGE",EDGE,{"disambiguationData":[OSD([sQuery(id+"F6.wireOp",EDGE,"E9.0.8.16")])],"isStart":true})});
            var Q179;
            Q179=makeQuery(id+"F7.boolean.opBoolean","COPY",EDGE,{"derivedFrom":makeQuery(id+"F7.opExtrude","CAP_EDGE",EDGE,{"disambiguationData":[OSD([sQuery(id+"F6.wireOp",EDGE,"E9.0.8.15")])],"isStart":true})});
            var Q180;
            Q180=makeQuery(id+"F7.boolean.opBoolean","COPY",EDGE,{"derivedFrom":makeQuery(id+"F7.opExtrude","CAP_EDGE",EDGE,{"disambiguationData":[OSD([sQuery(id+"F6.wireOp",EDGE,"E9.0.8.18")])],"isStart":false})});
            var Q181;
            Q181=makeQuery(id+"F7.boolean.opBoolean","COPY",EDGE,{"derivedFrom":makeQuery(id+"F7.opExtrude","CAP_EDGE",EDGE,{"disambiguationData":[OSD([sQuery(id+"F6.wireOp",EDGE,"E9.0.8.17")])],"isStart":false})});
            var Q182;
            Q182=makeQuery(id+"F7.boolean.opBoolean","COPY",EDGE,{"derivedFrom":makeQuery(id+"F7.opExtrude","CAP_EDGE",EDGE,{"disambiguationData":[OSD([sQuery(id+"F6.wireOp",EDGE,"E9.0.8.19")])],"isStart":false})});
            var Q183;
            Q183=makeQuery(id+"F7.boolean.opBoolean","COPY",EDGE,{"derivedFrom":makeQuery(id+"F7.opExtrude","CAP_EDGE",EDGE,{"disambiguationData":[OSD([sQuery(id+"F6.wireOp",EDGE,"E9.0.8.15")])],"isStart":false})});
            var Q184;
            Q184=makeQuery(id+"F7.boolean.opBoolean","COPY",EDGE,{"derivedFrom":makeQuery(id+"F7.opExtrude","CAP_EDGE",EDGE,{"disambiguationData":[OSD([sQuery(id+"F6.wireOp",EDGE,"E9.0.8.16")])],"isStart":false})});
            chamfer(context, id + "F8", {"entities" : qUnion([Q0, Q1, Q2, Q3, Q4, Q5, Q6, Q7, Q8, Q9, Q10, Q11, Q12, Q13, Q14, Q15, Q16, Q17, Q18, Q19, Q20, Q21, Q22, Q23, Q24, Q25, Q26, Q27, Q28, Q29, Q30, Q31, Q32, Q33, Q34, Q35, Q36, Q37, Q38, Q39, Q40, Q41, Q42, Q43, Q44, Q45, Q46, Q47, Q48, Q49, Q50, Q51, Q52, Q53, Q54, Q55, Q56, Q57, Q58, Q59, Q60, Q61, Q62, Q63, Q64, Q65, Q66, Q67, Q68, Q69, Q70, Q71, Q72, Q73, Q74, Q75, Q76, Q77, Q78, Q79, Q80, Q81, Q82, Q83, Q84, Q85, Q86, Q87, Q88, Q89, Q90, Q91, Q92, Q93, Q94, Q95, Q96, Q97, Q98, Q99, Q100, Q101, Q102, Q103, Q104, Q105, Q106, Q107, Q108, Q109, Q110, Q111, Q112, Q113, Q114, Q115, Q116, Q117, Q118, Q119, Q120, Q121, Q122, Q123, Q124, Q125, Q126, Q127, Q128, Q129, Q130, Q131, Q132, Q133, Q134, Q135, Q136, Q137, Q138, Q139, Q140, Q141, Q142, Q143, Q144, Q145, Q146, Q147, Q148, Q149, Q150, Q151, Q152, Q153, Q154, Q155, Q156, Q157, Q158, Q159, Q160, Q161, Q162, Q163, Q164, Q165, Q166, Q167, Q168, Q169, Q170, Q171, Q172, Q173, Q174, Q175, Q176, Q177, Q178, Q179, Q180, Q181, Q182, Q183, Q184]), "width" : 0.5 * mm, "tangentPropagation" : true});
        }
        {
            var Q0;
            Q0=qCreatedBy(makeId("Front.planeOp"),FACE);
            var sketch = newSketch(context, id + "F9", { "sketchPlane" : qUnion([Q0])});
            skLineSegment(sketch, "E10", {"start": v(0, 0) * mm, "end": v(0, -190.27) * mm, "construction": true});
            skSolve(sketch);
        }
        {
            var Q0;
            Q0=makeQuery(id+"F0.imprint","IMPRINT",FACE,{"disambiguationData":[TD([[makeQuery(id+"F0.imprint","IMPRINT",EDGE,{"derivedFrom":sQuery(id+"F0.wireOp",EDGE,"E0.bottom")}),1.0]])]});
            var sketch = newSketch(context, id + "F10", { "sketchPlane" : qUnion([Q0])});
            skLineSegment(sketch, "E11.bottom", {"start": v(-177.8, 177.8) * mm, "end": v(177.8, 177.8) * mm});
            skLineSegment(sketch, "E11.top", {"start": v(-177.8, -177.8) * mm, "end": v(177.8, -177.8) * mm});
            skLineSegment(sketch, "E11.left", {"start": v(-177.8, 177.8) * mm, "end": v(-177.8, -177.8) * mm});
            skLineSegment(sketch, "E11.right", {"start": v(177.8, 177.8) * mm, "end": v(177.8, -177.8) * mm});
            skPoint(sketch, "E11.middle", {"position": v(0, 0) * mm});
            skSolve(sketch);
        }
        {
            var Q0;
            Q0=qSketchRegion(id+"F10",true);
            var Q1;
            Q1=makeQuery(id+"F10.imprint","IMPRINT",FACE,{"disambiguationData":[TD([[makeQuery(id+"F10.imprint","IMPRINT",EDGE,{"derivedFrom":sQuery(id+"F10.wireOp",EDGE,"E11.bottom")}),-1.0]])]});
            extrude(context, id + "F11", {"entities" : qUnion([Q0, Q1]), "oppositeDirection" : true, "depth" : 139.7 * mm, "hasSecondDirection" : true, "secondDirectionOppositeDirection" : true, "secondDirectionDepth" : 63.5 * mm});
        }
        {
            var Q0;
            Q0=makeQuery(id+"F11.opExtrude","CAP_FACE",FACE,{"disambiguationData":[OSD([sQuery(id+"F10.wireOp",EDGE,"E11.bottom"),sQuery(id+"F10.wireOp",EDGE,"E11.top"),sQuery(id+"F10.wireOp",EDGE,"E11.left"),sQuery(id+"F10.wireOp",EDGE,"E11.right")])],"isStart":true});
            var Q1;
            Q1=makeQuery(id+"F11.opExtrude","CAP_FACE",FACE,{"disambiguationData":[OSD([sQuery(id+"F10.wireOp",EDGE,"E11.bottom"),sQuery(id+"F10.wireOp",EDGE,"E11.top"),sQuery(id+"F10.wireOp",EDGE,"E11.left"),sQuery(id+"F10.wireOp",EDGE,"E11.right")])],"isStart":false});
            chamfer(context, id + "F12", {"entities" : qUnion([Q0, Q1]), "width" : 3.17 * mm, "tangentPropagation" : true});
        }
        {
            var Q0;
            Q0=makeQuery(id+"F11.opExtrude","SWEPT_FACE",FACE,{"disambiguationData":[OSD([sQuery(id+"F10.wireOp",EDGE,"E11.bottom")])]});
            var sketch = newSketch(context, id + "F13", { "sketchPlane" : qUnion([Q0])});
            skLineSegment(sketch, "E12.bottom", {"start": v(-158.75, -38.1) * mm, "end": v(-44.45, -38.1) * mm});
            skLineSegment(sketch, "E12.top", {"start": v(-158.75, -101.6) * mm, "end": v(-44.45, -101.6) * mm});
            skLineSegment(sketch, "E12.left", {"start": v(-158.75, -38.1) * mm, "end": v(-158.75, -101.6) * mm});
            skLineSegment(sketch, "E12.right", {"start": v(-44.45, -38.1) * mm, "end": v(-44.45, -101.6) * mm});
            skPoint(sketch, "E12.middle", {"position": v(-109.84, -66.67) * mm});
            skCircle(sketch, "E13", {"center": v(-139.7, -82.55) * mm, "radius": 9.53 * mm});
            skCircle(sketch, "E14", {"center": v(-63.5, -82.55) * mm, "radius": 9.53 * mm});
            skCircle(sketch, "E15", {"center": v(-139.7, -82.55) * mm, "radius": 6.35 * mm});
            skCircle(sketch, "E16", {"center": v(-63.5, -82.55) * mm, "radius": 6.35 * mm});
            skLineSegment(sketch, "E17.MirrorCS", {"start": v(158.75, -38.1) * mm, "end": v(44.45, -38.1) * mm});
            skLineSegment(sketch, "E18.MirrorCS", {"start": v(44.45, -38.1) * mm, "end": v(44.45, -101.6) * mm});
            skLineSegment(sketch, "E19.MirrorCS", {"start": v(158.75, -101.6) * mm, "end": v(44.45, -101.6) * mm});
            skLineSegment(sketch, "E20.MirrorCS", {"start": v(158.75, -38.1) * mm, "end": v(158.75, -101.6) * mm});
            skCircle(sketch, "E21.MirrorC", {"center": v(139.7, -82.55) * mm, "radius": 9.53 * mm});
            skCircle(sketch, "E22.MirrorC", {"center": v(139.7, -82.55) * mm, "radius": 6.35 * mm});
            skCircle(sketch, "E23.MirrorC", {"center": v(63.5, -82.55) * mm, "radius": 9.53 * mm});
            skCircle(sketch, "E24.MirrorC", {"center": v(63.5, -82.55) * mm, "radius": 6.35 * mm});
            skSolve(sketch);
        }
        {
            var Q0;
            {var subQ1=sQuery(id+"F13.wireOp",EDGE,"E12.top");Q0=makeQuery(id+"F13.imprint","IMPRINT",FACE,{"disambiguationData":[TD([[makeQuery(id+"F13.imprint","IMPRINT",EDGE,{"derivedFrom":subQ1}),1.0]])]});}
            var Q1;
            {var subQ0=sQuery(id+"F13.wireOp",EDGE,"E12.bottom");Q1=makeQuery(id+"F13.imprint","IMPRINT",FACE,{"disambiguationData":[TD([[makeQuery(id+"F13.imprint","IMPRINT",EDGE,{"derivedFrom":subQ0}),-1.0]])]});}
            var Q2;
            {var subQ0=sQuery(id+"F13.wireOp",EDGE,"E17.MirrorCS");Q2=makeQuery(id+"F13.imprint","IMPRINT",FACE,{"disambiguationData":[TD([[makeQuery(id+"F13.imprint","IMPRINT",EDGE,{"derivedFrom":subQ0}),1.0]])]});}
            var Q3;
            {var subQ6=sQuery(id+"F13.wireOp",EDGE,"E19.MirrorCS");Q3=makeQuery(id+"F13.imprint","IMPRINT",FACE,{"disambiguationData":[TD([[makeQuery(id+"F13.imprint","IMPRINT",EDGE,{"derivedFrom":subQ6}),-1.0]])]});}
            var Q4;
            Q4=makeQuery(id+"F13.imprint","IMPRINT",FACE,{"disambiguationData":[TD([[makeQuery(id+"F13.imprint","IMPRINT",EDGE,{"derivedFrom":sQuery(id+"F13.wireOp",EDGE,"E23.MirrorC")}),-1.0]])]});
            var Q5;
            Q5=makeQuery(id+"F13.imprint","IMPRINT",FACE,{"disambiguationData":[TD([[makeQuery(id+"F13.imprint","IMPRINT",EDGE,{"derivedFrom":sQuery(id+"F13.wireOp",EDGE,"E14")}),1.0]])]});
            var Q6;
            Q6=makeQuery(id+"F13.imprint","IMPRINT",FACE,{"disambiguationData":[TD([[makeQuery(id+"F13.imprint","IMPRINT",EDGE,{"derivedFrom":sQuery(id+"F13.wireOp",EDGE,"E13")}),1.0]])]});
            var Q7;
            Q7=makeQuery(id+"F13.imprint","IMPRINT",FACE,{"disambiguationData":[TD([[makeQuery(id+"F13.imprint","IMPRINT",EDGE,{"derivedFrom":sQuery(id+"F13.wireOp",EDGE,"E21.MirrorC")}),-1.0]])]});
            extrude(context, id + "F14", {"entities" : qUnion([Q0, Q1, Q2, Q3, Q4, Q5, Q6, Q7]), "depth" : 15.88 * mm});
        }
        {
            var Q0;
            Q0=makeQuery(id+"F13.imprint","IMPRINT",FACE,{"disambiguationData":[TD([[makeQuery(id+"F13.imprint","IMPRINT",EDGE,{"derivedFrom":sQuery(id+"F13.wireOp",EDGE,"E13")}),1.0]])]});
            var Q1;
            Q1=makeQuery(id+"F13.imprint","IMPRINT",FACE,{"disambiguationData":[TD([[makeQuery(id+"F13.imprint","IMPRINT",EDGE,{"derivedFrom":sQuery(id+"F13.wireOp",EDGE,"E14")}),1.0]])]});
            var Q2;
            Q2=makeQuery(id+"F13.imprint","IMPRINT",FACE,{"disambiguationData":[TD([[makeQuery(id+"F13.imprint","IMPRINT",EDGE,{"derivedFrom":sQuery(id+"F13.wireOp",EDGE,"E23.MirrorC")}),-1.0]])]});
            var Q3;
            Q3=makeQuery(id+"F13.imprint","IMPRINT",FACE,{"disambiguationData":[TD([[makeQuery(id+"F13.imprint","IMPRINT",EDGE,{"derivedFrom":sQuery(id+"F13.wireOp",EDGE,"E21.MirrorC")}),-1.0]])]});
            extrude(context, id + "F15", {"entities" : qUnion([Q0, Q1, Q2, Q3]), "operationType" : NewBodyOperationType.REMOVE, "depth" : 25.4 * mm, "hasSecondDirection" : true, "secondDirectionOppositeDirection" : false, "secondDirectionDepth" : 3.17 * mm, "offsetDistance" : 25.4 * mm});
        }
        {
            var Q0;
            Q0=makeQuery(id+"F14.opExtrude","SWEPT_BODY",BODY,{"disambiguationData":[OSD([sQuery(id+"F13.wireOp",EDGE,"E12.bottom"),sQuery(id+"F13.wireOp",EDGE,"E12.top"),sQuery(id+"F13.wireOp",EDGE,"E12.left"),sQuery(id+"F13.wireOp",EDGE,"E12.right"),sQuery(id+"F13.wireOp",EDGE,"E15"),sQuery(id+"F13.wireOp",EDGE,"E16")])]});
            var Q1;
            Q1=makeQuery(id+"F14.opExtrude","SWEPT_BODY",BODY,{"disambiguationData":[OSD([sQuery(id+"F13.wireOp",EDGE,"E17.MirrorCS"),sQuery(id+"F13.wireOp",EDGE,"E18.MirrorCS"),sQuery(id+"F13.wireOp",EDGE,"E19.MirrorCS"),sQuery(id+"F13.wireOp",EDGE,"E20.MirrorCS"),sQuery(id+"F13.wireOp",EDGE,"E22.MirrorC"),sQuery(id+"F13.wireOp",EDGE,"E24.MirrorC")])]});
            var Q2;
            Q2=sQuery(id+"F9.wireOp",EDGE,"E10");
            circularPattern(context, id + "F16", {"entities" : qUnion([Q0, Q1]), "axis" : qUnion([Q2]), "angle" : 90 * degree, "instanceCount" : 2, "equalSpace" : true, "computeTransformsWithoutBuiltin" : true});
        }
        {
            var Q0;
            Q0=makeQuery(id+"F14.opExtrude","CAP_FACE",FACE,{"disambiguationData":[OSD([sQuery(id+"F13.wireOp",EDGE,"E12.bottom"),sQuery(id+"F13.wireOp",EDGE,"E12.top"),sQuery(id+"F13.wireOp",EDGE,"E12.left"),sQuery(id+"F13.wireOp",EDGE,"E12.right"),sQuery(id+"F13.wireOp",EDGE,"E15"),sQuery(id+"F13.wireOp",EDGE,"E16")])],"isStart":false});
            var Q1;
            Q1=makeQuery(id+"F14.opExtrude","CAP_FACE",FACE,{"disambiguationData":[OSD([sQuery(id+"F13.wireOp",EDGE,"E17.MirrorCS"),sQuery(id+"F13.wireOp",EDGE,"E18.MirrorCS"),sQuery(id+"F13.wireOp",EDGE,"E19.MirrorCS"),sQuery(id+"F13.wireOp",EDGE,"E20.MirrorCS"),sQuery(id+"F13.wireOp",EDGE,"E22.MirrorC"),sQuery(id+"F13.wireOp",EDGE,"E24.MirrorC")])],"isStart":false});
            var Q2;
            Q2=makeQuery(id+"F16.opPattern","COPY",FACE,{"derivedFrom":makeQuery(id+"F14.opExtrude","CAP_FACE",FACE,{"disambiguationData":[OSD([sQuery(id+"F13.wireOp",EDGE,"E17.MirrorCS"),sQuery(id+"F13.wireOp",EDGE,"E18.MirrorCS"),sQuery(id+"F13.wireOp",EDGE,"E19.MirrorCS"),sQuery(id+"F13.wireOp",EDGE,"E20.MirrorCS"),sQuery(id+"F13.wireOp",EDGE,"E22.MirrorC"),sQuery(id+"F13.wireOp",EDGE,"E24.MirrorC")])],"isStart":false}),"instanceName":"1"});
            var Q3;
            Q3=makeQuery(id+"F16.opPattern","COPY",FACE,{"derivedFrom":makeQuery(id+"F14.opExtrude","CAP_FACE",FACE,{"disambiguationData":[OSD([sQuery(id+"F13.wireOp",EDGE,"E12.bottom"),sQuery(id+"F13.wireOp",EDGE,"E12.top"),sQuery(id+"F13.wireOp",EDGE,"E12.left"),sQuery(id+"F13.wireOp",EDGE,"E12.right"),sQuery(id+"F13.wireOp",EDGE,"E15"),sQuery(id+"F13.wireOp",EDGE,"E16")])],"isStart":false}),"instanceName":"1"});
            var Q4;
            Q4=makeQuery(id+"F16.opPattern","COPY",EDGE,{"derivedFrom":makeQuery(id+"F14.opExtrude","SWEPT_EDGE",EDGE,{"disambiguationData":[OSD([sQuery(id+"F13.wireOp",EDGE,"E17.MirrorCS"),sQuery(id+"F13.wireOp",EDGE,"E20.MirrorCS")])]}),"instanceName":"1"});
            var Q5;
            Q5=makeQuery(id+"F16.opPattern","COPY",EDGE,{"derivedFrom":makeQuery(id+"F14.opExtrude","SWEPT_EDGE",EDGE,{"disambiguationData":[OSD([sQuery(id+"F13.wireOp",EDGE,"E17.MirrorCS"),sQuery(id+"F13.wireOp",EDGE,"E18.MirrorCS")])]}),"instanceName":"1"});
            var Q6;
            Q6=makeQuery(id+"F16.opPattern","COPY",EDGE,{"derivedFrom":makeQuery(id+"F14.opExtrude","SWEPT_EDGE",EDGE,{"disambiguationData":[OSD([sQuery(id+"F13.wireOp",EDGE,"E12.bottom"),sQuery(id+"F13.wireOp",EDGE,"E12.right")])]}),"instanceName":"1"});
            var Q7;
            Q7=makeQuery(id+"F16.opPattern","COPY",EDGE,{"derivedFrom":makeQuery(id+"F14.opExtrude","SWEPT_EDGE",EDGE,{"disambiguationData":[OSD([sQuery(id+"F13.wireOp",EDGE,"E12.bottom"),sQuery(id+"F13.wireOp",EDGE,"E12.left")])]}),"instanceName":"1"});
            var Q8;
            Q8=makeQuery(id+"F14.opExtrude","SWEPT_EDGE",EDGE,{"disambiguationData":[OSD([sQuery(id+"F13.wireOp",EDGE,"E12.bottom"),sQuery(id+"F13.wireOp",EDGE,"E12.left")])]});
            var Q9;
            Q9=makeQuery(id+"F14.opExtrude","SWEPT_EDGE",EDGE,{"disambiguationData":[OSD([sQuery(id+"F13.wireOp",EDGE,"E17.MirrorCS"),sQuery(id+"F13.wireOp",EDGE,"E18.MirrorCS")])]});
            var Q10;
            Q10=makeQuery(id+"F14.opExtrude","SWEPT_EDGE",EDGE,{"disambiguationData":[OSD([sQuery(id+"F13.wireOp",EDGE,"E17.MirrorCS"),sQuery(id+"F13.wireOp",EDGE,"E20.MirrorCS")])]});
            var Q11;
            Q11=makeQuery(id+"F14.opExtrude","SWEPT_EDGE",EDGE,{"disambiguationData":[OSD([sQuery(id+"F13.wireOp",EDGE,"E18.MirrorCS"),sQuery(id+"F13.wireOp",EDGE,"E19.MirrorCS")])]});
            var Q12;
            Q12=makeQuery(id+"F14.opExtrude","SWEPT_EDGE",EDGE,{"disambiguationData":[OSD([sQuery(id+"F13.wireOp",EDGE,"E19.MirrorCS"),sQuery(id+"F13.wireOp",EDGE,"E20.MirrorCS")])]});
            var Q13;
            Q13=makeQuery(id+"F14.opExtrude","SWEPT_EDGE",EDGE,{"disambiguationData":[OSD([sQuery(id+"F13.wireOp",EDGE,"E12.top"),sQuery(id+"F13.wireOp",EDGE,"E12.left")])]});
            var Q14;
            Q14=makeQuery(id+"F16.opPattern","COPY",EDGE,{"derivedFrom":makeQuery(id+"F14.opExtrude","SWEPT_EDGE",EDGE,{"disambiguationData":[OSD([sQuery(id+"F13.wireOp",EDGE,"E19.MirrorCS"),sQuery(id+"F13.wireOp",EDGE,"E20.MirrorCS")])]}),"instanceName":"1"});
            var Q15;
            Q15=makeQuery(id+"F16.opPattern","COPY",EDGE,{"derivedFrom":makeQuery(id+"F14.opExtrude","SWEPT_EDGE",EDGE,{"disambiguationData":[OSD([sQuery(id+"F13.wireOp",EDGE,"E18.MirrorCS"),sQuery(id+"F13.wireOp",EDGE,"E19.MirrorCS")])]}),"instanceName":"1"});
            var Q16;
            Q16=makeQuery(id+"F16.opPattern","COPY",EDGE,{"derivedFrom":makeQuery(id+"F14.opExtrude","SWEPT_EDGE",EDGE,{"disambiguationData":[OSD([sQuery(id+"F13.wireOp",EDGE,"E12.top"),sQuery(id+"F13.wireOp",EDGE,"E12.left")])]}),"instanceName":"1"});
            var Q17;
            Q17=makeQuery(id+"F16.opPattern","COPY",EDGE,{"derivedFrom":makeQuery(id+"F14.opExtrude","SWEPT_EDGE",EDGE,{"disambiguationData":[OSD([sQuery(id+"F13.wireOp",EDGE,"E12.top"),sQuery(id+"F13.wireOp",EDGE,"E12.right")])]}),"instanceName":"1"});
            var Q18;
            Q18=makeQuery(id+"F16.opPattern","COPY",EDGE,{"derivedFrom":makeQuery(id+"F14.opExtrude","CAP_EDGE",EDGE,{"disambiguationData":[OSD([sQuery(id+"F13.wireOp",EDGE,"E12.top")])],"isStart":true}),"instanceName":"1"});
            var Q19;
            Q19=makeQuery(id+"F16.opPattern","COPY",EDGE,{"derivedFrom":makeQuery(id+"F14.opExtrude","CAP_EDGE",EDGE,{"disambiguationData":[OSD([sQuery(id+"F13.wireOp",EDGE,"E12.left")])],"isStart":true}),"instanceName":"1"});
            var Q20;
            Q20=makeQuery(id+"F16.opPattern","COPY",EDGE,{"derivedFrom":makeQuery(id+"F14.opExtrude","CAP_EDGE",EDGE,{"disambiguationData":[OSD([sQuery(id+"F13.wireOp",EDGE,"E12.right")])],"isStart":true}),"instanceName":"1"});
            var Q21;
            Q21=makeQuery(id+"F16.opPattern","COPY",EDGE,{"derivedFrom":makeQuery(id+"F14.opExtrude","CAP_EDGE",EDGE,{"disambiguationData":[OSD([sQuery(id+"F13.wireOp",EDGE,"E12.bottom")])],"isStart":true}),"instanceName":"1"});
            var Q22;
            Q22=makeQuery(id+"F16.opPattern","COPY",EDGE,{"derivedFrom":makeQuery(id+"F14.opExtrude","CAP_EDGE",EDGE,{"disambiguationData":[OSD([sQuery(id+"F13.wireOp",EDGE,"E17.MirrorCS")])],"isStart":true}),"instanceName":"1"});
            var Q23;
            Q23=makeQuery(id+"F14.opExtrude","CAP_EDGE",EDGE,{"disambiguationData":[OSD([sQuery(id+"F13.wireOp",EDGE,"E12.bottom")])],"isStart":true});
            var Q24;
            Q24=makeQuery(id+"F14.opExtrude","CAP_EDGE",EDGE,{"disambiguationData":[OSD([sQuery(id+"F13.wireOp",EDGE,"E17.MirrorCS")])],"isStart":true});
            var Q25;
            Q25=makeQuery(id+"F14.opExtrude","CAP_EDGE",EDGE,{"disambiguationData":[OSD([sQuery(id+"F13.wireOp",EDGE,"E18.MirrorCS")])],"isStart":true});
            var Q26;
            Q26=makeQuery(id+"F14.opExtrude","CAP_EDGE",EDGE,{"disambiguationData":[OSD([sQuery(id+"F13.wireOp",EDGE,"E12.left")])],"isStart":true});
            var Q27;
            Q27=makeQuery(id+"F14.opExtrude","CAP_EDGE",EDGE,{"disambiguationData":[OSD([sQuery(id+"F13.wireOp",EDGE,"E12.right")])],"isStart":true});
            var Q28;
            Q28=makeQuery(id+"F14.opExtrude","CAP_EDGE",EDGE,{"disambiguationData":[OSD([sQuery(id+"F13.wireOp",EDGE,"E20.MirrorCS")])],"isStart":true});
            var Q29;
            Q29=makeQuery(id+"F14.opExtrude","CAP_EDGE",EDGE,{"disambiguationData":[OSD([sQuery(id+"F13.wireOp",EDGE,"E19.MirrorCS")])],"isStart":true});
            var Q30;
            Q30=makeQuery(id+"F14.opExtrude","CAP_EDGE",EDGE,{"disambiguationData":[OSD([sQuery(id+"F13.wireOp",EDGE,"E12.top")])],"isStart":true});
            var Q31;
            Q31=makeQuery(id+"F16.opPattern","COPY",EDGE,{"derivedFrom":makeQuery(id+"F14.opExtrude","CAP_EDGE",EDGE,{"disambiguationData":[OSD([sQuery(id+"F13.wireOp",EDGE,"E19.MirrorCS")])],"isStart":true}),"instanceName":"1"});
            var Q32;
            Q32=makeQuery(id+"F16.opPattern","COPY",EDGE,{"derivedFrom":makeQuery(id+"F14.opExtrude","CAP_EDGE",EDGE,{"disambiguationData":[OSD([sQuery(id+"F13.wireOp",EDGE,"E18.MirrorCS")])],"isStart":true}),"instanceName":"1"});
            var Q33;
            Q33=makeQuery(id+"F16.opPattern","COPY",EDGE,{"derivedFrom":makeQuery(id+"F14.opExtrude","CAP_EDGE",EDGE,{"disambiguationData":[OSD([sQuery(id+"F13.wireOp",EDGE,"E20.MirrorCS")])],"isStart":true}),"instanceName":"1"});
            chamfer(context, id + "F17", {"entities" : qUnion([Q0, Q1, Q2, Q3, Q4, Q5, Q6, Q7, Q8, Q9, Q10, Q11, Q12, Q13, Q14, Q15, Q16, Q17, Q18, Q19, Q20, Q21, Q22, Q23, Q24, Q25, Q26, Q27, Q28, Q29, Q30, Q31, Q32, Q33]), "width" : 1.27 * mm, "tangentPropagation" : true});
        }
        {
            var Q0;
            Q0=makeQuery(id+"F1.opExtrude","SWEPT_FACE",FACE,{"disambiguationData":[OSD([sQuery(id+"F0.wireOp",EDGE,"E0.right")])]});
            var sketch = newSketch(context, id + "F18", { "sketchPlane" : qUnion([Q0])});
            skLineSegment(sketch, "E25", {"start": v(-99.3, 37.72) * mm, "end": v(103.9, 37.72) * mm});
            skText(sketch, "E26", { "text": "SIDE A   G54", "fontName": "NotoSerif-Bold.ttf"});
            const initialGuessF18  = {"E26": [-0.0993, 0.02534, 1, 0, 0.02386]};
            skSetInitialGuess(sketch, initialGuessF18);
            skSolve(sketch);
        }
        {
            var Q0;
            Q0=qSketchRegion(id+"F18",true);
            extrude(context, id + "F19", {"entities" : qUnion([Q0]), "operationType" : NewBodyOperationType.ADD, "depth" : 0.76 * mm, "offsetDistance" : 25.4 * mm});
        }
    });
